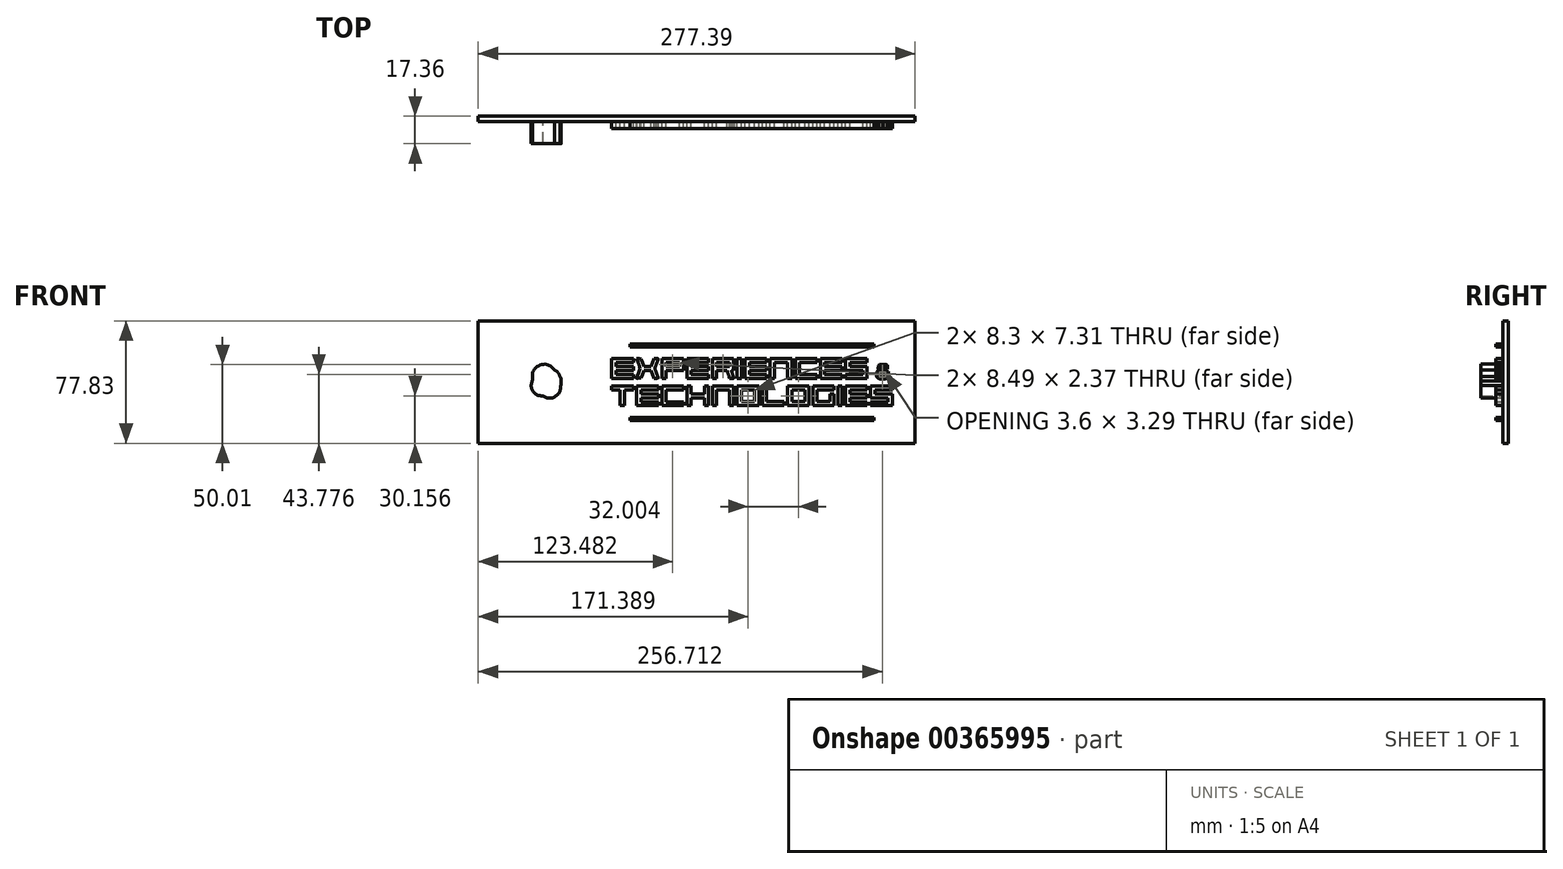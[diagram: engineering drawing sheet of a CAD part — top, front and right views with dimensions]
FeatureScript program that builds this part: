
annotation { "Feature Type Name" : "Feature", "Feature Type Description" : "" }
export const myFeature = defineFeature(function(context is Context, id is Id, definition is map)
    precondition{}
    {
        {
            var Q0;
            Q0=qCreatedBy(makeId("Front.planeOp"),FACE);
            var sketch = newSketch(context, id + "F0", { "sketchPlane" : qUnion([Q0])});
            skFitSpline(sketch, "E0", {"points": [v(-202.29, -52.1) * mm, v(-202.63, -51.97) * mm, v(-207.23, -47.55) * mm, v(-212.5, -42.27) * mm]});
            skLineSegment(sketch, "E1", {"start": v(-212.5, -42.27) * mm, "end": v(-222.07, -32.68) * mm});
            skLineSegment(sketch, "E2", {"start": v(-222.07, -32.68) * mm, "end": v(-222.07, 0) * mm});
            skLineSegment(sketch, "E3", {"start": v(-222.07, 0) * mm, "end": v(-222.06, 32.69) * mm});
            skLineSegment(sketch, "E4", {"start": v(-222.06, 32.69) * mm, "end": v(-212.25, 42.46) * mm});
            skLineSegment(sketch, "E5", {"start": v(-212.25, 42.46) * mm, "end": v(-202.45, 52.24) * mm});
            skLineSegment(sketch, "E6", {"start": v(-202.45, 52.24) * mm, "end": v(-163.97, 52.26) * mm});
            skFitSpline(sketch, "E7", {"points": [v(-163.97, 52.26) * mm, v(-141.12, 52.27) * mm, v(-125.15, 52.15) * mm, v(-124.66, 51.95) * mm]});
            skFitSpline(sketch, "E8", {"points": [v(-124.66, 51.95) * mm, v(-123.83, 51.63) * mm, v(-104.06, 32.01) * mm, v(-103.43, 30.9) * mm]});
            skFitSpline(sketch, "E9", {"points": [v(-103.43, 30.9) * mm, v(-103.17, 30.42) * mm, v(-104.47, 28.94) * mm, v(-110.36, 23.07) * mm]});
            skFitSpline(sketch, "E10", {"points": [v(-110.36, 23.07) * mm, v(-118.62, 14.84) * mm, v(-117.53, 15.3) * mm, v(-120.97, 18.54) * mm]});
            skFitSpline(sketch, "E11", {"points": [v(-120.97, 18.54) * mm, v(-124.99, 22.33) * mm, v(-133.5, 27.21) * mm, v(-139.35, 29.1) * mm]});
            skFitSpline(sketch, "E12", {"points": [v(-139.35, 29.1) * mm, v(-147.14, 31.6) * mm, v(-149.04, 31.85) * mm, v(-161.22, 32) * mm]});
            skFitSpline(sketch, "E13", {"points": [v(-161.22, 32) * mm, v(-175.01, 32.17) * mm, v(-177.89, 31.75) * mm, v(-184.15, 28.62) * mm]});
            skFitSpline(sketch, "E14", {"points": [v(-184.15, 28.62) * mm, v(-187.85, 26.77) * mm, v(-191.88, 23.86) * mm, v(-191.53, 23.3) * mm]});
            skFitSpline(sketch, "E15", {"points": [v(-191.53, 23.3) * mm, v(-191.42, 23.12) * mm, v(-191.5, 23.01) * mm, v(-191.7, 23.07) * mm]});
            skFitSpline(sketch, "E16", {"points": [v(-191.7, 23.07) * mm, v(-192.32, 23.23) * mm, v(-195.74, 19.26) * mm, v(-197.53, 16.3) * mm]});
            skFitSpline(sketch, "E17", {"points": [v(-197.53, 16.3) * mm, v(-203.86, 5.82) * mm, v(-203.4, -8.29) * mm, v(-196.42, -18.2) * mm]});
            skFitSpline(sketch, "E18", {"points": [v(-196.42, -18.2) * mm, v(-194.67, -20.7) * mm, v(-189.4, -26.05) * mm, v(-188.72, -26.05) * mm]});
            skFitSpline(sketch, "E19", {"points": [v(-188.72, -26.05) * mm, v(-188.47, -26.05) * mm, v(-188.21, -26.17) * mm, v(-188.15, -26.32) * mm]});
            skFitSpline(sketch, "E20", {"points": [v(-188.15, -26.32) * mm, v(-187.87, -26.95) * mm, v(-184.27, -28.92) * mm, v(-181.26, -30.08) * mm]});
            skFitSpline(sketch, "E21", {"points": [v(-181.26, -30.08) * mm, v(-176.54, -31.9) * mm, v(-172.16, -32.44) * mm, v(-162.45, -32.36) * mm]});
            skFitSpline(sketch, "E22", {"points": [v(-162.45, -32.36) * mm, v(-158.09, -32.32) * mm, v(-153.33, -32.15) * mm, v(-151.87, -31.98) * mm]});
            skFitSpline(sketch, "E23", {"points": [v(-151.87, -31.98) * mm, v(-139.35, -30.48) * mm, v(-129.8, -26.35) * mm, v(-120.76, -18.54) * mm]});
            skFitSpline(sketch, "E24", {"points": [v(-120.76, -18.54) * mm, v(-119.22, -17.21) * mm, v(-117.82, -16.18) * mm, v(-117.64, -16.24) * mm]});
            skFitSpline(sketch, "E25", {"points": [v(-117.64, -16.24) * mm, v(-117.06, -16.44) * mm, v(-103.55, -30.05) * mm, v(-103.37, -30.62) * mm]});
            skFitSpline(sketch, "E26", {"points": [v(-103.37, -30.62) * mm, v(-103.25, -31) * mm, v(-106.53, -34.5) * mm, v(-113.69, -41.67) * mm]});
            skLineSegment(sketch, "E27", {"start": v(-113.69, -41.67) * mm, "end": v(-124.19, -52.16) * mm});
            skLineSegment(sketch, "E28", {"start": v(-124.19, -52.16) * mm, "end": v(-162.92, -52.25) * mm});
            skFitSpline(sketch, "E29", {"points": [v(-162.92, -52.25) * mm, v(-184.22, -52.3) * mm, v(-201.94, -52.23) * mm, v(-202.29, -52.1) * mm]});
            skLineSegment(sketch, "E30", {"start": v(-202.29, -52.1) * mm, "end": v(-202.29, -52.1) * mm});
            skLineSegment(sketch, "E31", {"start": v(-75.67, -41.75) * mm, "end": v(-75.67, -40.16) * mm});
            skLineSegment(sketch, "E32", {"start": v(-75.67, -40.16) * mm, "end": v(62.8, -40.16) * mm});
            skLineSegment(sketch, "E33", {"start": v(62.8, -40.16) * mm, "end": v(201.26, -40.16) * mm});
            skLineSegment(sketch, "E34", {"start": v(201.26, -40.16) * mm, "end": v(201.26, -41.75) * mm});
            skLineSegment(sketch, "E35", {"start": v(201.26, -41.75) * mm, "end": v(201.26, -43.34) * mm});
            skLineSegment(sketch, "E36", {"start": v(201.26, -43.34) * mm, "end": v(62.8, -43.34) * mm});
            skLineSegment(sketch, "E37", {"start": v(62.8, -43.34) * mm, "end": v(-75.67, -43.34) * mm});
            skLineSegment(sketch, "E38", {"start": v(-75.67, -43.34) * mm, "end": v(-75.67, -41.75) * mm});
            skLineSegment(sketch, "E39", {"start": v(-86.6, -17.94) * mm, "end": v(-86.6, -9.12) * mm});
            skLineSegment(sketch, "E40", {"start": v(-86.6, -9.12) * mm, "end": v(-91.55, -9.12) * mm});
            skLineSegment(sketch, "E41", {"start": v(-91.55, -9.12) * mm, "end": v(-96.48, -9.12) * mm});
            skLineSegment(sketch, "E42", {"start": v(-96.48, -9.12) * mm, "end": v(-96.48, -6.82) * mm});
            skLineSegment(sketch, "E43", {"start": v(-96.48, -6.82) * mm, "end": v(-96.48, -4.53) * mm});
            skLineSegment(sketch, "E44", {"start": v(-96.48, -4.53) * mm, "end": v(-84.14, -4.53) * mm});
            skLineSegment(sketch, "E45", {"start": v(-84.14, -4.53) * mm, "end": v(-71.8, -4.53) * mm});
            skLineSegment(sketch, "E46", {"start": v(-71.8, -4.53) * mm, "end": v(-71.8, -6.82) * mm});
            skLineSegment(sketch, "E47", {"start": v(-71.8, -6.82) * mm, "end": v(-71.8, -9.12) * mm});
            skLineSegment(sketch, "E48", {"start": v(-71.8, -9.12) * mm, "end": v(-76.73, -9.12) * mm});
            skLineSegment(sketch, "E49", {"start": v(-76.73, -9.12) * mm, "end": v(-81.67, -9.12) * mm});
            skLineSegment(sketch, "E50", {"start": v(-81.67, -9.12) * mm, "end": v(-81.67, -17.94) * mm});
            skLineSegment(sketch, "E51", {"start": v(-81.67, -17.94) * mm, "end": v(-81.67, -26.76) * mm});
            skLineSegment(sketch, "E52", {"start": v(-81.67, -26.76) * mm, "end": v(-84.14, -26.76) * mm});
            skLineSegment(sketch, "E53", {"start": v(-84.14, -26.76) * mm, "end": v(-86.6, -26.76) * mm});
            skLineSegment(sketch, "E54", {"start": v(-86.6, -26.76) * mm, "end": v(-86.6, -17.94) * mm});
            skLineSegment(sketch, "E55", {"start": v(-67.9, -15.64) * mm, "end": v(-67.9, -4.53) * mm});
            skLineSegment(sketch, "E56", {"start": v(-67.9, -4.53) * mm, "end": v(-55.56, -4.53) * mm});
            skLineSegment(sketch, "E57", {"start": v(-55.56, -4.53) * mm, "end": v(-43.22, -4.53) * mm});
            skLineSegment(sketch, "E58", {"start": v(-43.22, -4.53) * mm, "end": v(-43.22, -6.82) * mm});
            skLineSegment(sketch, "E59", {"start": v(-43.22, -6.82) * mm, "end": v(-43.22, -9.12) * mm});
            skLineSegment(sketch, "E60", {"start": v(-43.22, -9.12) * mm, "end": v(-53.1, -9.12) * mm});
            skLineSegment(sketch, "E61", {"start": v(-53.1, -9.12) * mm, "end": v(-62.97, -9.12) * mm});
            skLineSegment(sketch, "E62", {"start": v(-62.97, -9.12) * mm, "end": v(-62.97, -11.23) * mm});
            skLineSegment(sketch, "E63", {"start": v(-62.97, -11.23) * mm, "end": v(-62.97, -13.35) * mm});
            skLineSegment(sketch, "E64", {"start": v(-62.97, -13.35) * mm, "end": v(-53.1, -13.35) * mm});
            skLineSegment(sketch, "E65", {"start": v(-53.1, -13.35) * mm, "end": v(-43.22, -13.35) * mm});
            skLineSegment(sketch, "E66", {"start": v(-43.22, -13.35) * mm, "end": v(-43.22, -15.64) * mm});
            skLineSegment(sketch, "E67", {"start": v(-43.22, -15.64) * mm, "end": v(-43.22, -17.94) * mm});
            skLineSegment(sketch, "E68", {"start": v(-43.22, -17.94) * mm, "end": v(-53.1, -17.94) * mm});
            skLineSegment(sketch, "E69", {"start": v(-53.1, -17.94) * mm, "end": v(-62.97, -17.94) * mm});
            skLineSegment(sketch, "E70", {"start": v(-62.97, -17.94) * mm, "end": v(-62.97, -20.23) * mm});
            skLineSegment(sketch, "E71", {"start": v(-62.97, -20.23) * mm, "end": v(-62.97, -22.52) * mm});
            skLineSegment(sketch, "E72", {"start": v(-62.97, -22.52) * mm, "end": v(-53.1, -22.52) * mm});
            skLineSegment(sketch, "E73", {"start": v(-53.1, -22.52) * mm, "end": v(-43.22, -22.52) * mm});
            skLineSegment(sketch, "E74", {"start": v(-43.22, -22.52) * mm, "end": v(-43.22, -24.64) * mm});
            skLineSegment(sketch, "E75", {"start": v(-43.22, -24.64) * mm, "end": v(-43.22, -26.76) * mm});
            skLineSegment(sketch, "E76", {"start": v(-43.22, -26.76) * mm, "end": v(-55.56, -26.76) * mm});
            skLineSegment(sketch, "E77", {"start": v(-55.56, -26.76) * mm, "end": v(-67.9, -26.76) * mm});
            skLineSegment(sketch, "E78", {"start": v(-67.9, -26.76) * mm, "end": v(-67.9, -15.64) * mm});
            skLineSegment(sketch, "E79", {"start": v(-39.33, -15.64) * mm, "end": v(-39.33, -4.53) * mm});
            skLineSegment(sketch, "E80", {"start": v(-39.33, -4.53) * mm, "end": v(-27.16, -4.53) * mm});
            skLineSegment(sketch, "E81", {"start": v(-27.16, -4.53) * mm, "end": v(-15, -4.53) * mm});
            skLineSegment(sketch, "E82", {"start": v(-15, -4.53) * mm, "end": v(-15, -6.82) * mm});
            skLineSegment(sketch, "E83", {"start": v(-15, -6.82) * mm, "end": v(-15, -9.12) * mm});
            skLineSegment(sketch, "E84", {"start": v(-15, -9.12) * mm, "end": v(-24.87, -9.12) * mm});
            skLineSegment(sketch, "E85", {"start": v(-24.87, -9.12) * mm, "end": v(-34.75, -9.12) * mm});
            skLineSegment(sketch, "E86", {"start": v(-34.75, -9.12) * mm, "end": v(-34.75, -15.82) * mm});
            skLineSegment(sketch, "E87", {"start": v(-34.75, -15.82) * mm, "end": v(-34.75, -22.52) * mm});
            skLineSegment(sketch, "E88", {"start": v(-34.75, -22.52) * mm, "end": v(-24.87, -22.52) * mm});
            skLineSegment(sketch, "E89", {"start": v(-24.87, -22.52) * mm, "end": v(-15, -22.52) * mm});
            skLineSegment(sketch, "E90", {"start": v(-15, -22.52) * mm, "end": v(-15, -24.64) * mm});
            skLineSegment(sketch, "E91", {"start": v(-15, -24.64) * mm, "end": v(-15, -26.76) * mm});
            skLineSegment(sketch, "E92", {"start": v(-15, -26.76) * mm, "end": v(-27.16, -26.76) * mm});
            skLineSegment(sketch, "E93", {"start": v(-27.16, -26.76) * mm, "end": v(-39.33, -26.76) * mm});
            skLineSegment(sketch, "E94", {"start": v(-39.33, -26.76) * mm, "end": v(-39.33, -15.64) * mm});
            skLineSegment(sketch, "E95", {"start": v(-10.76, -15.64) * mm, "end": v(-10.76, -4.53) * mm});
            skLineSegment(sketch, "E96", {"start": v(-10.76, -4.53) * mm, "end": v(-8.47, -4.53) * mm});
            skLineSegment(sketch, "E97", {"start": v(-8.47, -4.53) * mm, "end": v(-6.17, -4.53) * mm});
            skLineSegment(sketch, "E98", {"start": v(-6.17, -4.53) * mm, "end": v(-6.17, -8.94) * mm});
            skLineSegment(sketch, "E99", {"start": v(-6.17, -8.94) * mm, "end": v(-6.17, -13.35) * mm});
            skLineSegment(sketch, "E100", {"start": v(-6.17, -13.35) * mm, "end": v(1.41, -13.35) * mm});
            skLineSegment(sketch, "E101", {"start": v(1.41, -13.35) * mm, "end": v(9, -13.35) * mm});
            skLineSegment(sketch, "E102", {"start": v(9, -13.35) * mm, "end": v(9, -8.94) * mm});
            skLineSegment(sketch, "E103", {"start": v(9, -8.94) * mm, "end": v(9, -4.53) * mm});
            skLineSegment(sketch, "E104", {"start": v(9, -4.53) * mm, "end": v(11.29, -4.53) * mm});
            skLineSegment(sketch, "E105", {"start": v(11.29, -4.53) * mm, "end": v(13.58, -4.53) * mm});
            skLineSegment(sketch, "E106", {"start": v(13.58, -4.53) * mm, "end": v(13.58, -15.64) * mm});
            skLineSegment(sketch, "E107", {"start": v(13.58, -15.64) * mm, "end": v(13.58, -26.76) * mm});
            skLineSegment(sketch, "E108", {"start": v(13.58, -26.76) * mm, "end": v(11.29, -26.76) * mm});
            skLineSegment(sketch, "E109", {"start": v(11.29, -26.76) * mm, "end": v(9, -26.76) * mm});
            skLineSegment(sketch, "E110", {"start": v(9, -26.76) * mm, "end": v(9, -22.35) * mm});
            skLineSegment(sketch, "E111", {"start": v(9, -22.35) * mm, "end": v(9, -17.94) * mm});
            skLineSegment(sketch, "E112", {"start": v(9, -17.94) * mm, "end": v(1.41, -17.94) * mm});
            skLineSegment(sketch, "E113", {"start": v(1.41, -17.94) * mm, "end": v(-6.17, -17.94) * mm});
            skLineSegment(sketch, "E114", {"start": v(-6.17, -17.94) * mm, "end": v(-6.17, -22.35) * mm});
            skLineSegment(sketch, "E115", {"start": v(-6.17, -22.35) * mm, "end": v(-6.17, -26.76) * mm});
            skLineSegment(sketch, "E116", {"start": v(-6.17, -26.76) * mm, "end": v(-8.47, -26.76) * mm});
            skLineSegment(sketch, "E117", {"start": v(-8.47, -26.76) * mm, "end": v(-10.76, -26.76) * mm});
            skLineSegment(sketch, "E118", {"start": v(-10.76, -26.76) * mm, "end": v(-10.76, -15.64) * mm});
            skLineSegment(sketch, "E119", {"start": v(17.82, -15.64) * mm, "end": v(17.82, -4.53) * mm});
            skLineSegment(sketch, "E120", {"start": v(17.82, -4.53) * mm, "end": v(29.99, -4.53) * mm});
            skLineSegment(sketch, "E121", {"start": v(29.99, -4.53) * mm, "end": v(42.16, -4.53) * mm});
            skLineSegment(sketch, "E122", {"start": v(42.16, -4.53) * mm, "end": v(42.16, -15.64) * mm});
            skLineSegment(sketch, "E123", {"start": v(42.16, -15.64) * mm, "end": v(42.16, -26.76) * mm});
            skLineSegment(sketch, "E124", {"start": v(42.16, -26.76) * mm, "end": v(39.86, -26.76) * mm});
            skLineSegment(sketch, "E125", {"start": v(39.86, -26.76) * mm, "end": v(37.57, -26.76) * mm});
            skLineSegment(sketch, "E126", {"start": v(37.57, -26.76) * mm, "end": v(37.57, -17.94) * mm});
            skLineSegment(sketch, "E127", {"start": v(37.57, -17.94) * mm, "end": v(37.57, -9.12) * mm});
            skLineSegment(sketch, "E128", {"start": v(37.57, -9.12) * mm, "end": v(29.99, -9.12) * mm});
            skLineSegment(sketch, "E129", {"start": v(29.99, -9.12) * mm, "end": v(22.4, -9.12) * mm});
            skLineSegment(sketch, "E130", {"start": v(22.4, -9.12) * mm, "end": v(22.4, -17.94) * mm});
            skLineSegment(sketch, "E131", {"start": v(22.4, -17.94) * mm, "end": v(22.4, -26.76) * mm});
            skLineSegment(sketch, "E132", {"start": v(22.4, -26.76) * mm, "end": v(20.1, -26.76) * mm});
            skLineSegment(sketch, "E133", {"start": v(20.1, -26.76) * mm, "end": v(17.82, -26.76) * mm});
            skLineSegment(sketch, "E134", {"start": v(17.82, -26.76) * mm, "end": v(17.82, -15.64) * mm});
            skLineSegment(sketch, "E135", {"start": v(46.04, -15.64) * mm, "end": v(46.04, -4.53) * mm});
            skLineSegment(sketch, "E136", {"start": v(46.04, -4.53) * mm, "end": v(58.38, -4.53) * mm});
            skLineSegment(sketch, "E137", {"start": v(58.38, -4.53) * mm, "end": v(70.73, -4.53) * mm});
            skLineSegment(sketch, "E138", {"start": v(70.73, -4.53) * mm, "end": v(70.73, -15.64) * mm});
            skLineSegment(sketch, "E139", {"start": v(70.73, -15.64) * mm, "end": v(70.73, -26.76) * mm});
            skLineSegment(sketch, "E140", {"start": v(70.73, -26.76) * mm, "end": v(58.38, -26.76) * mm});
            skLineSegment(sketch, "E141", {"start": v(58.38, -26.76) * mm, "end": v(46.04, -26.76) * mm});
            skLineSegment(sketch, "E142", {"start": v(46.04, -26.76) * mm, "end": v(46.04, -15.64) * mm});
            skLineSegment(sketch, "E143", {"start": v(65.8, -15.64) * mm, "end": v(65.8, -9.12) * mm});
            skLineSegment(sketch, "E144", {"start": v(65.8, -9.12) * mm, "end": v(58.38, -9.12) * mm});
            skLineSegment(sketch, "E145", {"start": v(58.38, -9.12) * mm, "end": v(50.98, -9.12) * mm});
            skLineSegment(sketch, "E146", {"start": v(50.98, -9.12) * mm, "end": v(50.98, -15.64) * mm});
            skLineSegment(sketch, "E147", {"start": v(50.98, -15.64) * mm, "end": v(50.98, -22.17) * mm});
            skLineSegment(sketch, "E148", {"start": v(50.98, -22.17) * mm, "end": v(58.38, -22.17) * mm});
            skLineSegment(sketch, "E149", {"start": v(58.38, -22.17) * mm, "end": v(65.8, -22.17) * mm});
            skLineSegment(sketch, "E150", {"start": v(65.8, -22.17) * mm, "end": v(65.8, -15.64) * mm});
            skLineSegment(sketch, "E151", {"start": v(74.61, -15.64) * mm, "end": v(74.61, -4.53) * mm});
            skLineSegment(sketch, "E152", {"start": v(74.61, -4.53) * mm, "end": v(77.08, -4.53) * mm});
            skLineSegment(sketch, "E153", {"start": v(77.08, -4.53) * mm, "end": v(79.55, -4.53) * mm});
            skLineSegment(sketch, "E154", {"start": v(79.55, -4.53) * mm, "end": v(79.55, -13.35) * mm});
            skLineSegment(sketch, "E155", {"start": v(79.55, -13.35) * mm, "end": v(79.55, -22.17) * mm});
            skLineSegment(sketch, "E156", {"start": v(79.55, -22.17) * mm, "end": v(89.43, -22.17) * mm});
            skLineSegment(sketch, "E157", {"start": v(89.43, -22.17) * mm, "end": v(99.3, -22.17) * mm});
            skLineSegment(sketch, "E158", {"start": v(99.3, -22.17) * mm, "end": v(99.3, -24.46) * mm});
            skLineSegment(sketch, "E159", {"start": v(99.3, -24.46) * mm, "end": v(99.3, -26.76) * mm});
            skLineSegment(sketch, "E160", {"start": v(99.3, -26.76) * mm, "end": v(86.96, -26.76) * mm});
            skLineSegment(sketch, "E161", {"start": v(86.96, -26.76) * mm, "end": v(74.61, -26.76) * mm});
            skLineSegment(sketch, "E162", {"start": v(74.61, -26.76) * mm, "end": v(74.61, -15.64) * mm});
            skLineSegment(sketch, "E163", {"start": v(103.19, -15.64) * mm, "end": v(103.19, -4.53) * mm});
            skLineSegment(sketch, "E164", {"start": v(103.19, -4.53) * mm, "end": v(115.36, -4.53) * mm});
            skLineSegment(sketch, "E165", {"start": v(115.36, -4.53) * mm, "end": v(127.53, -4.53) * mm});
            skLineSegment(sketch, "E166", {"start": v(127.53, -4.53) * mm, "end": v(127.53, -15.64) * mm});
            skLineSegment(sketch, "E167", {"start": v(127.53, -15.64) * mm, "end": v(127.53, -26.76) * mm});
            skLineSegment(sketch, "E168", {"start": v(127.53, -26.76) * mm, "end": v(115.36, -26.76) * mm});
            skLineSegment(sketch, "E169", {"start": v(115.36, -26.76) * mm, "end": v(103.19, -26.76) * mm});
            skLineSegment(sketch, "E170", {"start": v(103.19, -26.76) * mm, "end": v(103.19, -15.64) * mm});
            skLineSegment(sketch, "E171", {"start": v(122.94, -15.64) * mm, "end": v(122.94, -9.12) * mm});
            skLineSegment(sketch, "E172", {"start": v(122.94, -9.12) * mm, "end": v(115.53, -9.12) * mm});
            skLineSegment(sketch, "E173", {"start": v(115.53, -9.12) * mm, "end": v(108.13, -9.12) * mm});
            skLineSegment(sketch, "E174", {"start": v(108.13, -9.12) * mm, "end": v(108.13, -15.64) * mm});
            skLineSegment(sketch, "E175", {"start": v(108.13, -15.64) * mm, "end": v(108.13, -22.17) * mm});
            skLineSegment(sketch, "E176", {"start": v(108.13, -22.17) * mm, "end": v(115.53, -22.17) * mm});
            skLineSegment(sketch, "E177", {"start": v(115.53, -22.17) * mm, "end": v(122.94, -22.17) * mm});
            skLineSegment(sketch, "E178", {"start": v(122.94, -22.17) * mm, "end": v(122.94, -15.64) * mm});
            skLineSegment(sketch, "E179", {"start": v(131.76, -15.64) * mm, "end": v(131.76, -4.53) * mm});
            skLineSegment(sketch, "E180", {"start": v(131.76, -4.53) * mm, "end": v(143.93, -4.53) * mm});
            skLineSegment(sketch, "E181", {"start": v(143.93, -4.53) * mm, "end": v(156.1, -4.53) * mm});
            skLineSegment(sketch, "E182", {"start": v(156.1, -4.53) * mm, "end": v(156.1, -6.82) * mm});
            skLineSegment(sketch, "E183", {"start": v(156.1, -6.82) * mm, "end": v(156.1, -9.12) * mm});
            skLineSegment(sketch, "E184", {"start": v(156.1, -9.12) * mm, "end": v(146.23, -9.12) * mm});
            skLineSegment(sketch, "E185", {"start": v(146.23, -9.12) * mm, "end": v(136.35, -9.12) * mm});
            skLineSegment(sketch, "E186", {"start": v(136.35, -9.12) * mm, "end": v(136.35, -15.64) * mm});
            skLineSegment(sketch, "E187", {"start": v(136.35, -15.64) * mm, "end": v(136.35, -22.17) * mm});
            skLineSegment(sketch, "E188", {"start": v(136.35, -22.17) * mm, "end": v(143.93, -22.17) * mm});
            skLineSegment(sketch, "E189", {"start": v(143.93, -22.17) * mm, "end": v(151.52, -22.17) * mm});
            skLineSegment(sketch, "E190", {"start": v(151.52, -22.17) * mm, "end": v(151.52, -17.76) * mm});
            skLineSegment(sketch, "E191", {"start": v(151.52, -17.76) * mm, "end": v(151.52, -13.35) * mm});
            skLineSegment(sketch, "E192", {"start": v(151.52, -13.35) * mm, "end": v(153.81, -13.35) * mm});
            skLineSegment(sketch, "E193", {"start": v(153.81, -13.35) * mm, "end": v(156.1, -13.35) * mm});
            skLineSegment(sketch, "E194", {"start": v(156.1, -13.35) * mm, "end": v(156.1, -20.05) * mm});
            skLineSegment(sketch, "E195", {"start": v(156.1, -20.05) * mm, "end": v(156.1, -26.76) * mm});
            skLineSegment(sketch, "E196", {"start": v(156.1, -26.76) * mm, "end": v(143.93, -26.76) * mm});
            skLineSegment(sketch, "E197", {"start": v(143.93, -26.76) * mm, "end": v(131.76, -26.76) * mm});
            skLineSegment(sketch, "E198", {"start": v(131.76, -26.76) * mm, "end": v(131.76, -15.64) * mm});
            skLineSegment(sketch, "E199", {"start": v(160.34, -15.64) * mm, "end": v(160.34, -4.53) * mm});
            skLineSegment(sketch, "E200", {"start": v(160.34, -4.53) * mm, "end": v(162.63, -4.53) * mm});
            skLineSegment(sketch, "E201", {"start": v(162.63, -4.53) * mm, "end": v(164.92, -4.53) * mm});
            skLineSegment(sketch, "E202", {"start": v(164.92, -4.53) * mm, "end": v(164.92, -15.64) * mm});
            skLineSegment(sketch, "E203", {"start": v(164.92, -15.64) * mm, "end": v(164.92, -26.76) * mm});
            skLineSegment(sketch, "E204", {"start": v(164.92, -26.76) * mm, "end": v(162.63, -26.76) * mm});
            skLineSegment(sketch, "E205", {"start": v(162.63, -26.76) * mm, "end": v(160.34, -26.76) * mm});
            skLineSegment(sketch, "E206", {"start": v(160.34, -26.76) * mm, "end": v(160.34, -15.64) * mm});
            skLineSegment(sketch, "E207", {"start": v(169.16, -15.64) * mm, "end": v(169.16, -4.53) * mm});
            skLineSegment(sketch, "E208", {"start": v(169.16, -4.53) * mm, "end": v(181.33, -4.53) * mm});
            skLineSegment(sketch, "E209", {"start": v(181.33, -4.53) * mm, "end": v(193.5, -4.53) * mm});
            skLineSegment(sketch, "E210", {"start": v(193.5, -4.53) * mm, "end": v(193.5, -6.82) * mm});
            skLineSegment(sketch, "E211", {"start": v(193.5, -6.82) * mm, "end": v(193.5, -9.12) * mm});
            skLineSegment(sketch, "E212", {"start": v(193.5, -9.12) * mm, "end": v(183.62, -9.12) * mm});
            skLineSegment(sketch, "E213", {"start": v(183.62, -9.12) * mm, "end": v(173.74, -9.12) * mm});
            skLineSegment(sketch, "E214", {"start": v(173.74, -9.12) * mm, "end": v(173.74, -11.23) * mm});
            skLineSegment(sketch, "E215", {"start": v(173.74, -11.23) * mm, "end": v(173.74, -13.35) * mm});
            skLineSegment(sketch, "E216", {"start": v(173.74, -13.35) * mm, "end": v(183.62, -13.35) * mm});
            skLineSegment(sketch, "E217", {"start": v(183.62, -13.35) * mm, "end": v(193.5, -13.35) * mm});
            skLineSegment(sketch, "E218", {"start": v(193.5, -13.35) * mm, "end": v(193.5, -15.64) * mm});
            skLineSegment(sketch, "E219", {"start": v(193.5, -15.64) * mm, "end": v(193.5, -17.94) * mm});
            skLineSegment(sketch, "E220", {"start": v(193.5, -17.94) * mm, "end": v(183.62, -17.94) * mm});
            skLineSegment(sketch, "E221", {"start": v(183.62, -17.94) * mm, "end": v(173.74, -17.94) * mm});
            skLineSegment(sketch, "E222", {"start": v(173.74, -17.94) * mm, "end": v(173.74, -20.23) * mm});
            skLineSegment(sketch, "E223", {"start": v(173.74, -20.23) * mm, "end": v(173.74, -22.52) * mm});
            skLineSegment(sketch, "E224", {"start": v(173.74, -22.52) * mm, "end": v(183.62, -22.52) * mm});
            skLineSegment(sketch, "E225", {"start": v(183.62, -22.52) * mm, "end": v(193.5, -22.52) * mm});
            skLineSegment(sketch, "E226", {"start": v(193.5, -22.52) * mm, "end": v(193.5, -24.64) * mm});
            skLineSegment(sketch, "E227", {"start": v(193.5, -24.64) * mm, "end": v(193.5, -26.76) * mm});
            skLineSegment(sketch, "E228", {"start": v(193.5, -26.76) * mm, "end": v(181.33, -26.76) * mm});
            skLineSegment(sketch, "E229", {"start": v(181.33, -26.76) * mm, "end": v(169.16, -26.76) * mm});
            skLineSegment(sketch, "E230", {"start": v(169.16, -26.76) * mm, "end": v(169.16, -15.64) * mm});
            skLineSegment(sketch, "E231", {"start": v(197.38, -24.64) * mm, "end": v(197.38, -22.52) * mm});
            skLineSegment(sketch, "E232", {"start": v(197.38, -22.52) * mm, "end": v(207.26, -22.52) * mm});
            skLineSegment(sketch, "E233", {"start": v(207.26, -22.52) * mm, "end": v(217.13, -22.52) * mm});
            skLineSegment(sketch, "E234", {"start": v(217.13, -22.52) * mm, "end": v(217.13, -20.23) * mm});
            skLineSegment(sketch, "E235", {"start": v(217.13, -20.23) * mm, "end": v(217.13, -17.94) * mm});
            skLineSegment(sketch, "E236", {"start": v(217.13, -17.94) * mm, "end": v(207.26, -17.94) * mm});
            skLineSegment(sketch, "E237", {"start": v(207.26, -17.94) * mm, "end": v(197.38, -17.94) * mm});
            skLineSegment(sketch, "E238", {"start": v(197.38, -17.94) * mm, "end": v(197.38, -11.23) * mm});
            skLineSegment(sketch, "E239", {"start": v(197.38, -11.23) * mm, "end": v(197.38, -4.53) * mm});
            skLineSegment(sketch, "E240", {"start": v(197.38, -4.53) * mm, "end": v(209.73, -4.53) * mm});
            skLineSegment(sketch, "E241", {"start": v(209.73, -4.53) * mm, "end": v(222.07, -4.53) * mm});
            skLineSegment(sketch, "E242", {"start": v(222.07, -4.53) * mm, "end": v(222.07, -6.82) * mm});
            skLineSegment(sketch, "E243", {"start": v(222.07, -6.82) * mm, "end": v(222.07, -9.12) * mm});
            skLineSegment(sketch, "E244", {"start": v(222.07, -9.12) * mm, "end": v(212.2, -9.12) * mm});
            skLineSegment(sketch, "E245", {"start": v(212.2, -9.12) * mm, "end": v(202.32, -9.12) * mm});
            skLineSegment(sketch, "E246", {"start": v(202.32, -9.12) * mm, "end": v(202.32, -11.23) * mm});
            skLineSegment(sketch, "E247", {"start": v(202.32, -11.23) * mm, "end": v(202.32, -13.35) * mm});
            skLineSegment(sketch, "E248", {"start": v(202.32, -13.35) * mm, "end": v(212.2, -13.35) * mm});
            skLineSegment(sketch, "E249", {"start": v(212.2, -13.35) * mm, "end": v(222.07, -13.35) * mm});
            skLineSegment(sketch, "E250", {"start": v(222.07, -13.35) * mm, "end": v(222.07, -20.05) * mm});
            skLineSegment(sketch, "E251", {"start": v(222.07, -20.05) * mm, "end": v(222.07, -26.76) * mm});
            skLineSegment(sketch, "E252", {"start": v(222.07, -26.76) * mm, "end": v(209.73, -26.76) * mm});
            skLineSegment(sketch, "E253", {"start": v(209.73, -26.76) * mm, "end": v(197.38, -26.76) * mm});
            skLineSegment(sketch, "E254", {"start": v(197.38, -26.76) * mm, "end": v(197.38, -24.64) * mm});
            skFitSpline(sketch, "E255", {"points": [v(-174.06, -15.97) * mm, v(-182.2, -13.78) * mm, v(-187.45, -5.82) * mm, v(-186.12, 2.32) * mm]});
            skFitSpline(sketch, "E256", {"points": [v(-186.12, 2.32) * mm, v(-184.17, 14.28) * mm, v(-171, 20.11) * mm, v(-160.84, 13.53) * mm]});
            skFitSpline(sketch, "E257", {"points": [v(-160.84, 13.53) * mm, v(-158.3, 11.88) * mm, v(-156.44, 9.67) * mm, v(-154.98, 6.56) * mm]});
            skFitSpline(sketch, "E258", {"points": [v(-154.98, 6.56) * mm, v(-154.07, 4.61) * mm, v(-153.86, 3.64) * mm, v(-153.71, 0.9) * mm]});
            skFitSpline(sketch, "E259", {"points": [v(-153.71, 0.9) * mm, v(-153.6, -1.2) * mm, v(-153.7, -3) * mm, v(-154, -4.08) * mm]});
            skFitSpline(sketch, "E260", {"points": [v(-154, -4.08) * mm, v(-156.34, -12.87) * mm, v(-165.48, -18.27) * mm, v(-174.06, -15.97) * mm]});
            skFitSpline(sketch, "E261", {"points": [v(206.94, 4.04) * mm, v(205.13, 4.68) * mm, v(204.38, 5.93) * mm, v(204.32, 8.41) * mm]});
            skFitSpline(sketch, "E262", {"points": [v(204.32, 8.41) * mm, v(204.27, 10.71) * mm, v(205, 12.34) * mm, v(206.25, 12.67) * mm]});
            skFitSpline(sketch, "E263", {"points": [v(206.25, 12.67) * mm, v(206.73, 12.8) * mm, v(206.87, 13.03) * mm, v(206.7, 13.42) * mm]});
            skFitSpline(sketch, "E264", {"points": [v(206.7, 13.42) * mm, v(205.82, 15.53) * mm, v(205.78, 15.8) * mm, v(206.18, 17.28) * mm]});
            skFitSpline(sketch, "E265", {"points": [v(206.18, 17.28) * mm, v(206.7, 19.18) * mm, v(207.97, 19.81) * mm, v(211.32, 19.81) * mm]});
            skFitSpline(sketch, "E266", {"points": [v(211.32, 19.81) * mm, v(215.03, 19.81) * mm, v(216.43, 18.75) * mm, v(216.43, 15.95) * mm]});
            skLineSegment(sketch, "E267", {"start": v(216.43, 15.95) * mm, "end": v(216.43, 14.52) * mm});
            skLineSegment(sketch, "E268", {"start": v(216.43, 14.52) * mm, "end": v(214.84, 14.52) * mm});
            skFitSpline(sketch, "E269", {"points": [v(214.84, 14.52) * mm, v(213.26, 14.52) * mm, v(213.25, 14.53) * mm, v(213.25, 15.75) * mm]});
            skFitSpline(sketch, "E270", {"points": [v(213.25, 15.75) * mm, v(213.25, 16.78) * mm, v(213.1, 17.01) * mm, v(212.32, 17.2) * mm]});
            skFitSpline(sketch, "E271", {"points": [v(212.32, 17.2) * mm, v(210.78, 17.6) * mm, v(209.57, 16.96) * mm, v(209.44, 15.7) * mm]});
            skFitSpline(sketch, "E272", {"points": [v(209.44, 15.7) * mm, v(209.35, 14.72) * mm, v(209.62, 14.36) * mm, v(212.09, 12.24) * mm]});
            skFitSpline(sketch, "E273", {"points": [v(212.09, 12.24) * mm, v(214.75, 9.96) * mm, v(214.85, 9.91) * mm, v(214.95, 10.79) * mm]});
            skFitSpline(sketch, "E274", {"points": [v(214.95, 10.79) * mm, v(215.05, 11.6) * mm, v(215.22, 11.7) * mm, v(216.48, 11.7) * mm]});
            skLineSegment(sketch, "E275", {"start": v(216.48, 11.7) * mm, "end": v(217.9, 11.7) * mm});
            skLineSegment(sketch, "E276", {"start": v(217.9, 11.7) * mm, "end": v(217.8, 9.53) * mm});
            skFitSpline(sketch, "E277", {"points": [v(217.8, 9.53) * mm, v(217.72, 7.55) * mm, v(217.8, 7.32) * mm, v(218.66, 6.68) * mm]});
            skFitSpline(sketch, "E278", {"points": [v(218.66, 6.68) * mm, v(219.78, 5.87) * mm, v(219.82, 5.46) * mm, v(218.88, 4.33) * mm]});
            skLineSegment(sketch, "E279", {"start": v(218.88, 4.33) * mm, "end": v(218.17, 3.48) * mm});
            skLineSegment(sketch, "E280", {"start": v(218.17, 3.48) * mm, "end": v(217.37, 4.23) * mm});
            skLineSegment(sketch, "E281", {"start": v(217.37, 4.23) * mm, "end": v(216.57, 4.99) * mm});
            skLineSegment(sketch, "E282", {"start": v(216.57, 4.99) * mm, "end": v(215.19, 4.29) * mm});
            skFitSpline(sketch, "E283", {"points": [v(215.19, 4.29) * mm, v(213.59, 3.47) * mm, v(208.96, 3.33) * mm, v(206.94, 4.04) * mm]});
            skFitSpline(sketch, "E284", {"points": [v(213.05, 6.4) * mm, v(213.55, 6.59) * mm, v(213.95, 6.86) * mm, v(213.94, 7.01) * mm]});
            skFitSpline(sketch, "E285", {"points": [v(213.94, 7.01) * mm, v(213.92, 7.28) * mm, v(210.1, 10.53) * mm, v(209.12, 11.1) * mm]});
            skFitSpline(sketch, "E286", {"points": [v(209.12, 11.1) * mm, v(208.26, 11.62) * mm, v(207.6, 10.67) * mm, v(207.62, 8.92) * mm]});
            skFitSpline(sketch, "E287", {"points": [v(207.62, 8.92) * mm, v(207.62, 8.02) * mm, v(207.74, 7.1) * mm, v(207.88, 6.89) * mm]});
            skFitSpline(sketch, "E288", {"points": [v(207.88, 6.89) * mm, v(208.39, 6.1) * mm, v(211.5, 5.8) * mm, v(213.05, 6.4) * mm]});
            skLineSegment(sketch, "E289", {"start": v(-96.48, 15.4) * mm, "end": v(-96.48, 26.51) * mm});
            skLineSegment(sketch, "E290", {"start": v(-96.48, 26.51) * mm, "end": v(-84.14, 26.51) * mm});
            skLineSegment(sketch, "E291", {"start": v(-84.14, 26.51) * mm, "end": v(-71.8, 26.51) * mm});
            skLineSegment(sketch, "E292", {"start": v(-71.8, 26.51) * mm, "end": v(-71.8, 24.22) * mm});
            skLineSegment(sketch, "E293", {"start": v(-71.8, 24.22) * mm, "end": v(-71.8, 21.93) * mm});
            skLineSegment(sketch, "E294", {"start": v(-71.8, 21.93) * mm, "end": v(-81.67, 21.93) * mm});
            skLineSegment(sketch, "E295", {"start": v(-81.67, 21.93) * mm, "end": v(-91.55, 21.93) * mm});
            skLineSegment(sketch, "E296", {"start": v(-91.55, 21.93) * mm, "end": v(-91.55, 19.81) * mm});
            skLineSegment(sketch, "E297", {"start": v(-91.55, 19.81) * mm, "end": v(-91.55, 17.7) * mm});
            skLineSegment(sketch, "E298", {"start": v(-91.55, 17.7) * mm, "end": v(-81.67, 17.7) * mm});
            skLineSegment(sketch, "E299", {"start": v(-81.67, 17.7) * mm, "end": v(-71.8, 17.7) * mm});
            skLineSegment(sketch, "E300", {"start": v(-71.8, 17.7) * mm, "end": v(-71.8, 15.4) * mm});
            skLineSegment(sketch, "E301", {"start": v(-71.8, 15.4) * mm, "end": v(-71.8, 13.1) * mm});
            skLineSegment(sketch, "E302", {"start": v(-71.8, 13.1) * mm, "end": v(-81.67, 13.1) * mm});
            skLineSegment(sketch, "E303", {"start": v(-81.67, 13.1) * mm, "end": v(-91.55, 13.1) * mm});
            skLineSegment(sketch, "E304", {"start": v(-91.55, 13.1) * mm, "end": v(-91.55, 10.82) * mm});
            skLineSegment(sketch, "E305", {"start": v(-91.55, 10.82) * mm, "end": v(-91.55, 8.52) * mm});
            skLineSegment(sketch, "E306", {"start": v(-91.55, 8.52) * mm, "end": v(-81.67, 8.52) * mm});
            skLineSegment(sketch, "E307", {"start": v(-81.67, 8.52) * mm, "end": v(-71.8, 8.52) * mm});
            skLineSegment(sketch, "E308", {"start": v(-71.8, 8.52) * mm, "end": v(-71.8, 6.4) * mm});
            skLineSegment(sketch, "E309", {"start": v(-71.8, 6.4) * mm, "end": v(-71.8, 4.29) * mm});
            skLineSegment(sketch, "E310", {"start": v(-71.8, 4.29) * mm, "end": v(-84.14, 4.29) * mm});
            skLineSegment(sketch, "E311", {"start": v(-84.14, 4.29) * mm, "end": v(-96.48, 4.29) * mm});
            skLineSegment(sketch, "E312", {"start": v(-96.48, 4.29) * mm, "end": v(-96.48, 15.4) * mm});
            skFitSpline(sketch, "E313", {"points": [v(-67.83, 4.71) * mm, v(-67.74, 4.96) * mm, v(-66.82, 7.45) * mm, v(-65.8, 10.24) * mm]});
            skLineSegment(sketch, "E314", {"start": v(-65.8, 10.24) * mm, "end": v(-63.92, 15.3) * mm});
            skLineSegment(sketch, "E315", {"start": v(-63.92, 15.3) * mm, "end": v(-64.46, 16.94) * mm});
            skFitSpline(sketch, "E316", {"points": [v(-64.46, 16.94) * mm, v(-64.76, 17.84) * mm, v(-65.66, 20.37) * mm, v(-66.45, 22.56) * mm]});
            skLineSegment(sketch, "E317", {"start": v(-66.45, 22.56) * mm, "end": v(-67.9, 26.54) * mm});
            skLineSegment(sketch, "E318", {"start": v(-67.9, 26.54) * mm, "end": v(-65.37, 26.44) * mm});
            skLineSegment(sketch, "E319", {"start": v(-65.37, 26.44) * mm, "end": v(-62.84, 26.34) * mm});
            skLineSegment(sketch, "E320", {"start": v(-62.84, 26.34) * mm, "end": v(-61.25, 22) * mm});
            skLineSegment(sketch, "E321", {"start": v(-61.25, 22) * mm, "end": v(-59.67, 17.67) * mm});
            skLineSegment(sketch, "E322", {"start": v(-59.67, 17.67) * mm, "end": v(-55.59, 17.77) * mm});
            skLineSegment(sketch, "E323", {"start": v(-55.59, 17.77) * mm, "end": v(-51.5, 17.87) * mm});
            skLineSegment(sketch, "E324", {"start": v(-51.5, 17.87) * mm, "end": v(-49.96, 22.2) * mm});
            skLineSegment(sketch, "E325", {"start": v(-49.96, 22.2) * mm, "end": v(-48.4, 26.51) * mm});
            skLineSegment(sketch, "E326", {"start": v(-48.4, 26.51) * mm, "end": v(-45.99, 26.51) * mm});
            skFitSpline(sketch, "E327", {"points": [v(-45.99, 26.51) * mm, v(-44.66, 26.51) * mm, v(-43.57, 26.37) * mm, v(-43.57, 26.2) * mm]});
            skFitSpline(sketch, "E328", {"points": [v(-43.57, 26.2) * mm, v(-43.57, 26.01) * mm, v(-44.38, 23.67) * mm, v(-45.37, 20.99) * mm]});
            skFitSpline(sketch, "E329", {"points": [v(-45.37, 20.99) * mm, v(-46.35, 18.3) * mm, v(-47.16, 15.79) * mm, v(-47.16, 15.4) * mm]});
            skFitSpline(sketch, "E330", {"points": [v(-47.16, 15.4) * mm, v(-47.16, 15.01) * mm, v(-46.35, 12.5) * mm, v(-45.37, 9.81) * mm]});
            skFitSpline(sketch, "E331", {"points": [v(-45.37, 9.81) * mm, v(-44.38, 7.13) * mm, v(-43.57, 4.79) * mm, v(-43.57, 4.61) * mm]});
            skFitSpline(sketch, "E332", {"points": [v(-43.57, 4.61) * mm, v(-43.57, 4.43) * mm, v(-44.65, 4.29) * mm, v(-45.97, 4.29) * mm]});
            skLineSegment(sketch, "E333", {"start": v(-45.97, 4.29) * mm, "end": v(-48.37, 4.29) * mm});
            skLineSegment(sketch, "E334", {"start": v(-48.37, 4.29) * mm, "end": v(-49.94, 8.7) * mm});
            skLineSegment(sketch, "E335", {"start": v(-49.94, 8.7) * mm, "end": v(-51.5, 13.1) * mm});
            skLineSegment(sketch, "E336", {"start": v(-51.5, 13.1) * mm, "end": v(-55.6, 13.1) * mm});
            skLineSegment(sketch, "E337", {"start": v(-55.6, 13.1) * mm, "end": v(-59.7, 13.1) * mm});
            skLineSegment(sketch, "E338", {"start": v(-59.7, 13.1) * mm, "end": v(-61.27, 8.79) * mm});
            skLineSegment(sketch, "E339", {"start": v(-61.27, 8.79) * mm, "end": v(-62.85, 4.47) * mm});
            skLineSegment(sketch, "E340", {"start": v(-62.85, 4.47) * mm, "end": v(-65.42, 4.36) * mm});
            skFitSpline(sketch, "E341", {"points": [v(-65.42, 4.36) * mm, v(-67.42, 4.28) * mm, v(-67.96, 4.36) * mm, v(-67.83, 4.71) * mm]});
            skLineSegment(sketch, "E342", {"start": v(-67.83, 4.71) * mm, "end": v(-67.83, 4.71) * mm});
            skLineSegment(sketch, "E343", {"start": v(-39.33, 15.4) * mm, "end": v(-39.33, 26.51) * mm});
            skLineSegment(sketch, "E344", {"start": v(-39.33, 26.51) * mm, "end": v(-27.16, 26.51) * mm});
            skLineSegment(sketch, "E345", {"start": v(-27.16, 26.51) * mm, "end": v(-15, 26.51) * mm});
            skLineSegment(sketch, "E346", {"start": v(-15, 26.51) * mm, "end": v(-15, 19.81) * mm});
            skLineSegment(sketch, "E347", {"start": v(-15, 19.81) * mm, "end": v(-15, 13.1) * mm});
            skLineSegment(sketch, "E348", {"start": v(-15, 13.1) * mm, "end": v(-24.87, 13.1) * mm});
            skLineSegment(sketch, "E349", {"start": v(-24.87, 13.1) * mm, "end": v(-34.75, 13.1) * mm});
            skLineSegment(sketch, "E350", {"start": v(-34.75, 13.1) * mm, "end": v(-34.75, 8.7) * mm});
            skLineSegment(sketch, "E351", {"start": v(-34.75, 8.7) * mm, "end": v(-34.75, 4.29) * mm});
            skLineSegment(sketch, "E352", {"start": v(-34.75, 4.29) * mm, "end": v(-37.04, 4.29) * mm});
            skLineSegment(sketch, "E353", {"start": v(-37.04, 4.29) * mm, "end": v(-39.33, 4.29) * mm});
            skLineSegment(sketch, "E354", {"start": v(-39.33, 4.29) * mm, "end": v(-39.33, 15.4) * mm});
            skLineSegment(sketch, "E355", {"start": v(-19.58, 19.81) * mm, "end": v(-19.58, 21.93) * mm});
            skLineSegment(sketch, "E356", {"start": v(-19.58, 21.93) * mm, "end": v(-27.16, 21.93) * mm});
            skLineSegment(sketch, "E357", {"start": v(-27.16, 21.93) * mm, "end": v(-34.75, 21.93) * mm});
            skLineSegment(sketch, "E358", {"start": v(-34.75, 21.93) * mm, "end": v(-34.75, 19.81) * mm});
            skLineSegment(sketch, "E359", {"start": v(-34.75, 19.81) * mm, "end": v(-34.75, 17.7) * mm});
            skLineSegment(sketch, "E360", {"start": v(-34.75, 17.7) * mm, "end": v(-27.16, 17.7) * mm});
            skLineSegment(sketch, "E361", {"start": v(-27.16, 17.7) * mm, "end": v(-19.58, 17.7) * mm});
            skLineSegment(sketch, "E362", {"start": v(-19.58, 17.7) * mm, "end": v(-19.58, 19.81) * mm});
            skLineSegment(sketch, "E363", {"start": v(-10.76, 15.4) * mm, "end": v(-10.76, 26.51) * mm});
            skLineSegment(sketch, "E364", {"start": v(-10.76, 26.51) * mm, "end": v(1.41, 26.51) * mm});
            skLineSegment(sketch, "E365", {"start": v(1.41, 26.51) * mm, "end": v(13.58, 26.51) * mm});
            skLineSegment(sketch, "E366", {"start": v(13.58, 26.51) * mm, "end": v(13.58, 24.22) * mm});
            skLineSegment(sketch, "E367", {"start": v(13.58, 24.22) * mm, "end": v(13.58, 21.93) * mm});
            skLineSegment(sketch, "E368", {"start": v(13.58, 21.93) * mm, "end": v(3.7, 21.93) * mm});
            skLineSegment(sketch, "E369", {"start": v(3.7, 21.93) * mm, "end": v(-6.17, 21.93) * mm});
            skLineSegment(sketch, "E370", {"start": v(-6.17, 21.93) * mm, "end": v(-6.17, 19.81) * mm});
            skLineSegment(sketch, "E371", {"start": v(-6.17, 19.81) * mm, "end": v(-6.17, 17.7) * mm});
            skLineSegment(sketch, "E372", {"start": v(-6.17, 17.7) * mm, "end": v(3.7, 17.7) * mm});
            skLineSegment(sketch, "E373", {"start": v(3.7, 17.7) * mm, "end": v(13.58, 17.7) * mm});
            skLineSegment(sketch, "E374", {"start": v(13.58, 17.7) * mm, "end": v(13.58, 15.4) * mm});
            skLineSegment(sketch, "E375", {"start": v(13.58, 15.4) * mm, "end": v(13.58, 13.1) * mm});
            skLineSegment(sketch, "E376", {"start": v(13.58, 13.1) * mm, "end": v(3.7, 13.1) * mm});
            skLineSegment(sketch, "E377", {"start": v(3.7, 13.1) * mm, "end": v(-6.17, 13.1) * mm});
            skLineSegment(sketch, "E378", {"start": v(-6.17, 13.1) * mm, "end": v(-6.17, 10.82) * mm});
            skLineSegment(sketch, "E379", {"start": v(-6.17, 10.82) * mm, "end": v(-6.17, 8.52) * mm});
            skLineSegment(sketch, "E380", {"start": v(-6.17, 8.52) * mm, "end": v(3.7, 8.52) * mm});
            skLineSegment(sketch, "E381", {"start": v(3.7, 8.52) * mm, "end": v(13.58, 8.52) * mm});
            skLineSegment(sketch, "E382", {"start": v(13.58, 8.52) * mm, "end": v(13.58, 6.4) * mm});
            skLineSegment(sketch, "E383", {"start": v(13.58, 6.4) * mm, "end": v(13.58, 4.29) * mm});
            skLineSegment(sketch, "E384", {"start": v(13.58, 4.29) * mm, "end": v(1.41, 4.29) * mm});
            skLineSegment(sketch, "E385", {"start": v(1.41, 4.29) * mm, "end": v(-10.76, 4.29) * mm});
            skLineSegment(sketch, "E386", {"start": v(-10.76, 4.29) * mm, "end": v(-10.76, 15.4) * mm});
            skLineSegment(sketch, "E387", {"start": v(17.82, 15.4) * mm, "end": v(17.82, 26.51) * mm});
            skLineSegment(sketch, "E388", {"start": v(17.82, 26.51) * mm, "end": v(29.99, 26.51) * mm});
            skLineSegment(sketch, "E389", {"start": v(29.99, 26.51) * mm, "end": v(42.16, 26.51) * mm});
            skLineSegment(sketch, "E390", {"start": v(42.16, 26.51) * mm, "end": v(42.16, 19.81) * mm});
            skLineSegment(sketch, "E391", {"start": v(42.16, 19.81) * mm, "end": v(42.16, 13.1) * mm});
            skLineSegment(sketch, "E392", {"start": v(42.16, 13.1) * mm, "end": v(40.92, 13.1) * mm});
            skFitSpline(sketch, "E393", {"points": [v(40.92, 13.1) * mm, v(40.24, 13.1) * mm, v(39.69, 13.02) * mm, v(39.69, 12.92) * mm]});
            skFitSpline(sketch, "E394", {"points": [v(39.69, 12.92) * mm, v(39.69, 12.77) * mm, v(41.33, 7.1) * mm, v(42.01, 4.9) * mm]});
            skFitSpline(sketch, "E395", {"points": [v(42.01, 4.9) * mm, v(42.18, 4.36) * mm, v(41.93, 4.29) * mm, v(39.75, 4.29) * mm]});
            skLineSegment(sketch, "E396", {"start": v(39.75, 4.29) * mm, "end": v(37.29, 4.29) * mm});
            skLineSegment(sketch, "E397", {"start": v(37.29, 4.29) * mm, "end": v(36.52, 6.85) * mm});
            skFitSpline(sketch, "E398", {"points": [v(36.52, 6.85) * mm, v(36.1, 8.25) * mm, v(35.5, 10.24) * mm, v(35.19, 11.26) * mm]});
            skLineSegment(sketch, "E399", {"start": v(35.19, 11.26) * mm, "end": v(34.62, 13.1) * mm});
            skLineSegment(sketch, "E400", {"start": v(34.62, 13.1) * mm, "end": v(28.51, 13.1) * mm});
            skLineSegment(sketch, "E401", {"start": v(28.51, 13.1) * mm, "end": v(22.4, 13.1) * mm});
            skLineSegment(sketch, "E402", {"start": v(22.4, 13.1) * mm, "end": v(22.4, 8.7) * mm});
            skLineSegment(sketch, "E403", {"start": v(22.4, 8.7) * mm, "end": v(22.4, 4.29) * mm});
            skLineSegment(sketch, "E404", {"start": v(22.4, 4.29) * mm, "end": v(20.1, 4.29) * mm});
            skLineSegment(sketch, "E405", {"start": v(20.1, 4.29) * mm, "end": v(17.82, 4.29) * mm});
            skLineSegment(sketch, "E406", {"start": v(17.82, 4.29) * mm, "end": v(17.82, 15.4) * mm});
            skLineSegment(sketch, "E407", {"start": v(37.57, 19.81) * mm, "end": v(37.57, 21.93) * mm});
            skLineSegment(sketch, "E408", {"start": v(37.57, 21.93) * mm, "end": v(29.99, 21.93) * mm});
            skLineSegment(sketch, "E409", {"start": v(29.99, 21.93) * mm, "end": v(22.4, 21.93) * mm});
            skLineSegment(sketch, "E410", {"start": v(22.4, 21.93) * mm, "end": v(22.4, 19.81) * mm});
            skLineSegment(sketch, "E411", {"start": v(22.4, 19.81) * mm, "end": v(22.4, 17.7) * mm});
            skLineSegment(sketch, "E412", {"start": v(22.4, 17.7) * mm, "end": v(29.99, 17.7) * mm});
            skLineSegment(sketch, "E413", {"start": v(29.99, 17.7) * mm, "end": v(37.57, 17.7) * mm});
            skLineSegment(sketch, "E414", {"start": v(37.57, 17.7) * mm, "end": v(37.57, 19.81) * mm});
            skLineSegment(sketch, "E415", {"start": v(46.04, 15.4) * mm, "end": v(46.04, 26.51) * mm});
            skLineSegment(sketch, "E416", {"start": v(46.04, 26.51) * mm, "end": v(48.5, 26.51) * mm});
            skLineSegment(sketch, "E417", {"start": v(48.5, 26.51) * mm, "end": v(50.98, 26.51) * mm});
            skLineSegment(sketch, "E418", {"start": v(50.98, 26.51) * mm, "end": v(50.98, 15.4) * mm});
            skLineSegment(sketch, "E419", {"start": v(50.98, 15.4) * mm, "end": v(50.98, 4.29) * mm});
            skLineSegment(sketch, "E420", {"start": v(50.98, 4.29) * mm, "end": v(48.5, 4.29) * mm});
            skLineSegment(sketch, "E421", {"start": v(48.5, 4.29) * mm, "end": v(46.04, 4.29) * mm});
            skLineSegment(sketch, "E422", {"start": v(46.04, 4.29) * mm, "end": v(46.04, 15.4) * mm});
            skLineSegment(sketch, "E423", {"start": v(54.86, 15.4) * mm, "end": v(54.86, 26.51) * mm});
            skLineSegment(sketch, "E424", {"start": v(54.86, 26.51) * mm, "end": v(67.2, 26.51) * mm});
            skLineSegment(sketch, "E425", {"start": v(67.2, 26.51) * mm, "end": v(79.55, 26.51) * mm});
            skLineSegment(sketch, "E426", {"start": v(79.55, 26.51) * mm, "end": v(79.55, 24.22) * mm});
            skLineSegment(sketch, "E427", {"start": v(79.55, 24.22) * mm, "end": v(79.55, 21.93) * mm});
            skLineSegment(sketch, "E428", {"start": v(79.55, 21.93) * mm, "end": v(69.67, 21.93) * mm});
            skLineSegment(sketch, "E429", {"start": v(69.67, 21.93) * mm, "end": v(59.8, 21.93) * mm});
            skLineSegment(sketch, "E430", {"start": v(59.8, 21.93) * mm, "end": v(59.8, 19.81) * mm});
            skLineSegment(sketch, "E431", {"start": v(59.8, 19.81) * mm, "end": v(59.8, 17.7) * mm});
            skLineSegment(sketch, "E432", {"start": v(59.8, 17.7) * mm, "end": v(69.67, 17.7) * mm});
            skLineSegment(sketch, "E433", {"start": v(69.67, 17.7) * mm, "end": v(79.55, 17.7) * mm});
            skLineSegment(sketch, "E434", {"start": v(79.55, 17.7) * mm, "end": v(79.55, 15.4) * mm});
            skLineSegment(sketch, "E435", {"start": v(79.55, 15.4) * mm, "end": v(79.55, 13.1) * mm});
            skLineSegment(sketch, "E436", {"start": v(79.55, 13.1) * mm, "end": v(69.67, 13.1) * mm});
            skLineSegment(sketch, "E437", {"start": v(69.67, 13.1) * mm, "end": v(59.8, 13.1) * mm});
            skLineSegment(sketch, "E438", {"start": v(59.8, 13.1) * mm, "end": v(59.8, 10.82) * mm});
            skLineSegment(sketch, "E439", {"start": v(59.8, 10.82) * mm, "end": v(59.8, 8.52) * mm});
            skLineSegment(sketch, "E440", {"start": v(59.8, 8.52) * mm, "end": v(69.67, 8.52) * mm});
            skLineSegment(sketch, "E441", {"start": v(69.67, 8.52) * mm, "end": v(79.55, 8.52) * mm});
            skLineSegment(sketch, "E442", {"start": v(79.55, 8.52) * mm, "end": v(79.55, 6.4) * mm});
            skLineSegment(sketch, "E443", {"start": v(79.55, 6.4) * mm, "end": v(79.55, 4.29) * mm});
            skLineSegment(sketch, "E444", {"start": v(79.55, 4.29) * mm, "end": v(67.2, 4.29) * mm});
            skLineSegment(sketch, "E445", {"start": v(67.2, 4.29) * mm, "end": v(54.86, 4.29) * mm});
            skLineSegment(sketch, "E446", {"start": v(54.86, 4.29) * mm, "end": v(54.86, 15.4) * mm});
            skLineSegment(sketch, "E447", {"start": v(83.43, 15.4) * mm, "end": v(83.43, 26.51) * mm});
            skLineSegment(sketch, "E448", {"start": v(83.43, 26.51) * mm, "end": v(95.78, 26.51) * mm});
            skLineSegment(sketch, "E449", {"start": v(95.78, 26.51) * mm, "end": v(108.13, 26.51) * mm});
            skLineSegment(sketch, "E450", {"start": v(108.13, 26.51) * mm, "end": v(108.13, 15.4) * mm});
            skLineSegment(sketch, "E451", {"start": v(108.13, 15.4) * mm, "end": v(108.13, 4.29) * mm});
            skLineSegment(sketch, "E452", {"start": v(108.13, 4.29) * mm, "end": v(105.66, 4.29) * mm});
            skLineSegment(sketch, "E453", {"start": v(105.66, 4.29) * mm, "end": v(103.19, 4.29) * mm});
            skLineSegment(sketch, "E454", {"start": v(103.19, 4.29) * mm, "end": v(103.19, 13.1) * mm});
            skLineSegment(sketch, "E455", {"start": v(103.19, 13.1) * mm, "end": v(103.19, 21.93) * mm});
            skLineSegment(sketch, "E456", {"start": v(103.19, 21.93) * mm, "end": v(95.78, 21.93) * mm});
            skLineSegment(sketch, "E457", {"start": v(95.78, 21.93) * mm, "end": v(88.37, 21.93) * mm});
            skLineSegment(sketch, "E458", {"start": v(88.37, 21.93) * mm, "end": v(88.37, 13.1) * mm});
            skLineSegment(sketch, "E459", {"start": v(88.37, 13.1) * mm, "end": v(88.37, 4.29) * mm});
            skLineSegment(sketch, "E460", {"start": v(88.37, 4.29) * mm, "end": v(85.9, 4.29) * mm});
            skLineSegment(sketch, "E461", {"start": v(85.9, 4.29) * mm, "end": v(83.43, 4.29) * mm});
            skLineSegment(sketch, "E462", {"start": v(83.43, 4.29) * mm, "end": v(83.43, 15.4) * mm});
            skLineSegment(sketch, "E463", {"start": v(112, 15.4) * mm, "end": v(112, 26.51) * mm});
            skLineSegment(sketch, "E464", {"start": v(112, 26.51) * mm, "end": v(124.18, 26.51) * mm});
            skLineSegment(sketch, "E465", {"start": v(124.18, 26.51) * mm, "end": v(136.35, 26.51) * mm});
            skLineSegment(sketch, "E466", {"start": v(136.35, 26.51) * mm, "end": v(136.35, 24.22) * mm});
            skLineSegment(sketch, "E467", {"start": v(136.35, 24.22) * mm, "end": v(136.35, 21.93) * mm});
            skLineSegment(sketch, "E468", {"start": v(136.35, 21.93) * mm, "end": v(126.47, 21.93) * mm});
            skLineSegment(sketch, "E469", {"start": v(126.47, 21.93) * mm, "end": v(116.6, 21.93) * mm});
            skLineSegment(sketch, "E470", {"start": v(116.6, 21.93) * mm, "end": v(116.6, 15.22) * mm});
            skLineSegment(sketch, "E471", {"start": v(116.6, 15.22) * mm, "end": v(116.6, 8.52) * mm});
            skLineSegment(sketch, "E472", {"start": v(116.6, 8.52) * mm, "end": v(126.47, 8.52) * mm});
            skLineSegment(sketch, "E473", {"start": v(126.47, 8.52) * mm, "end": v(136.35, 8.52) * mm});
            skLineSegment(sketch, "E474", {"start": v(136.35, 8.52) * mm, "end": v(136.35, 6.4) * mm});
            skLineSegment(sketch, "E475", {"start": v(136.35, 6.4) * mm, "end": v(136.35, 4.29) * mm});
            skLineSegment(sketch, "E476", {"start": v(136.35, 4.29) * mm, "end": v(124.18, 4.29) * mm});
            skLineSegment(sketch, "E477", {"start": v(124.18, 4.29) * mm, "end": v(112, 4.29) * mm});
            skLineSegment(sketch, "E478", {"start": v(112, 4.29) * mm, "end": v(112, 15.4) * mm});
            skLineSegment(sketch, "E479", {"start": v(140.58, 15.4) * mm, "end": v(140.58, 26.51) * mm});
            skLineSegment(sketch, "E480", {"start": v(140.58, 26.51) * mm, "end": v(152.75, 26.51) * mm});
            skLineSegment(sketch, "E481", {"start": v(152.75, 26.51) * mm, "end": v(164.92, 26.51) * mm});
            skLineSegment(sketch, "E482", {"start": v(164.92, 26.51) * mm, "end": v(164.92, 24.22) * mm});
            skLineSegment(sketch, "E483", {"start": v(164.92, 24.22) * mm, "end": v(164.92, 21.93) * mm});
            skLineSegment(sketch, "E484", {"start": v(164.92, 21.93) * mm, "end": v(155.05, 21.93) * mm});
            skLineSegment(sketch, "E485", {"start": v(155.05, 21.93) * mm, "end": v(145.17, 21.93) * mm});
            skLineSegment(sketch, "E486", {"start": v(145.17, 21.93) * mm, "end": v(145.17, 19.81) * mm});
            skLineSegment(sketch, "E487", {"start": v(145.17, 19.81) * mm, "end": v(145.17, 17.7) * mm});
            skLineSegment(sketch, "E488", {"start": v(145.17, 17.7) * mm, "end": v(155.05, 17.7) * mm});
            skLineSegment(sketch, "E489", {"start": v(155.05, 17.7) * mm, "end": v(164.92, 17.7) * mm});
            skLineSegment(sketch, "E490", {"start": v(164.92, 17.7) * mm, "end": v(164.92, 15.4) * mm});
            skLineSegment(sketch, "E491", {"start": v(164.92, 15.4) * mm, "end": v(164.92, 13.1) * mm});
            skLineSegment(sketch, "E492", {"start": v(164.92, 13.1) * mm, "end": v(155.05, 13.1) * mm});
            skLineSegment(sketch, "E493", {"start": v(155.05, 13.1) * mm, "end": v(145.17, 13.1) * mm});
            skLineSegment(sketch, "E494", {"start": v(145.17, 13.1) * mm, "end": v(145.17, 10.82) * mm});
            skLineSegment(sketch, "E495", {"start": v(145.17, 10.82) * mm, "end": v(145.17, 8.52) * mm});
            skLineSegment(sketch, "E496", {"start": v(145.17, 8.52) * mm, "end": v(155.05, 8.52) * mm});
            skLineSegment(sketch, "E497", {"start": v(155.05, 8.52) * mm, "end": v(164.92, 8.52) * mm});
            skLineSegment(sketch, "E498", {"start": v(164.92, 8.52) * mm, "end": v(164.92, 6.4) * mm});
            skLineSegment(sketch, "E499", {"start": v(164.92, 6.4) * mm, "end": v(164.92, 4.29) * mm});
            skLineSegment(sketch, "E500", {"start": v(164.92, 4.29) * mm, "end": v(152.75, 4.29) * mm});
            skLineSegment(sketch, "E501", {"start": v(152.75, 4.29) * mm, "end": v(140.58, 4.29) * mm});
            skLineSegment(sketch, "E502", {"start": v(140.58, 4.29) * mm, "end": v(140.58, 15.4) * mm});
            skLineSegment(sketch, "E503", {"start": v(169.16, 6.4) * mm, "end": v(169.16, 8.52) * mm});
            skLineSegment(sketch, "E504", {"start": v(169.16, 8.52) * mm, "end": v(179.03, 8.52) * mm});
            skLineSegment(sketch, "E505", {"start": v(179.03, 8.52) * mm, "end": v(188.91, 8.52) * mm});
            skLineSegment(sketch, "E506", {"start": v(188.91, 8.52) * mm, "end": v(188.91, 10.82) * mm});
            skLineSegment(sketch, "E507", {"start": v(188.91, 10.82) * mm, "end": v(188.91, 13.1) * mm});
            skLineSegment(sketch, "E508", {"start": v(188.91, 13.1) * mm, "end": v(179.03, 13.1) * mm});
            skLineSegment(sketch, "E509", {"start": v(179.03, 13.1) * mm, "end": v(169.16, 13.1) * mm});
            skLineSegment(sketch, "E510", {"start": v(169.16, 13.1) * mm, "end": v(169.16, 19.81) * mm});
            skLineSegment(sketch, "E511", {"start": v(169.16, 19.81) * mm, "end": v(169.16, 26.51) * mm});
            skLineSegment(sketch, "E512", {"start": v(169.16, 26.51) * mm, "end": v(181.33, 26.51) * mm});
            skLineSegment(sketch, "E513", {"start": v(181.33, 26.51) * mm, "end": v(193.5, 26.51) * mm});
            skLineSegment(sketch, "E514", {"start": v(193.5, 26.51) * mm, "end": v(193.5, 24.22) * mm});
            skLineSegment(sketch, "E515", {"start": v(193.5, 24.22) * mm, "end": v(193.5, 21.93) * mm});
            skLineSegment(sketch, "E516", {"start": v(193.5, 21.93) * mm, "end": v(183.62, 21.93) * mm});
            skLineSegment(sketch, "E517", {"start": v(183.62, 21.93) * mm, "end": v(173.74, 21.93) * mm});
            skLineSegment(sketch, "E518", {"start": v(173.74, 21.93) * mm, "end": v(173.74, 19.81) * mm});
            skLineSegment(sketch, "E519", {"start": v(173.74, 19.81) * mm, "end": v(173.74, 17.7) * mm});
            skLineSegment(sketch, "E520", {"start": v(173.74, 17.7) * mm, "end": v(183.62, 17.7) * mm});
            skLineSegment(sketch, "E521", {"start": v(183.62, 17.7) * mm, "end": v(193.5, 17.7) * mm});
            skLineSegment(sketch, "E522", {"start": v(193.5, 17.7) * mm, "end": v(193.5, 11) * mm});
            skLineSegment(sketch, "E523", {"start": v(193.5, 11) * mm, "end": v(193.5, 4.29) * mm});
            skLineSegment(sketch, "E524", {"start": v(193.5, 4.29) * mm, "end": v(181.33, 4.29) * mm});
            skLineSegment(sketch, "E525", {"start": v(181.33, 4.29) * mm, "end": v(169.16, 4.29) * mm});
            skLineSegment(sketch, "E526", {"start": v(169.16, 4.29) * mm, "end": v(169.16, 6.4) * mm});
            skLineSegment(sketch, "E527", {"start": v(-75.67, 41.5) * mm, "end": v(-75.67, 43.1) * mm});
            skLineSegment(sketch, "E528", {"start": v(-75.67, 43.1) * mm, "end": v(62.8, 43.1) * mm});
            skLineSegment(sketch, "E529", {"start": v(62.8, 43.1) * mm, "end": v(201.26, 43.1) * mm});
            skLineSegment(sketch, "E530", {"start": v(201.26, 43.1) * mm, "end": v(201.26, 41.5) * mm});
            skLineSegment(sketch, "E531", {"start": v(201.26, 41.5) * mm, "end": v(201.26, 39.92) * mm});
            skLineSegment(sketch, "E532", {"start": v(201.26, 39.92) * mm, "end": v(62.8, 39.92) * mm});
            skLineSegment(sketch, "E533", {"start": v(62.8, 39.92) * mm, "end": v(-75.67, 39.92) * mm});
            skLineSegment(sketch, "E534", {"start": v(-75.67, 39.92) * mm, "end": v(-75.67, 41.5) * mm});
            skLineSegment(sketch, "E535.bottom", {"start": v(247.67, 69.49) * mm, "end": v(-247.67, 69.49) * mm});
            skLineSegment(sketch, "E535.top", {"start": v(247.67, -69.49) * mm, "end": v(-247.67, -69.49) * mm});
            skLineSegment(sketch, "E535.left", {"start": v(247.67, 69.49) * mm, "end": v(247.67, -69.49) * mm});
            skLineSegment(sketch, "E535.right", {"start": v(-247.67, 69.49) * mm, "end": v(-247.67, -69.49) * mm});
            skPoint(sketch, "E535.middle", {"position": v(0, 0) * mm});
            skSolve(sketch);
        }
        {
            var Q0;
            Q0=makeQuery(id+"F0.imprint","IMPRINT",FACE,{"disambiguationData":[TD([[makeQuery(id+"F0.imprint","IMPRINT",EDGE,{"derivedFrom":sQuery(id+"F0.wireOp",EDGE,"E289")}),-1.0]])]});
            var Q1;
            Q1=makeQuery(id+"F0.imprint","IMPRINT",FACE,{"disambiguationData":[TD([[makeQuery(id+"F0.imprint","IMPRINT",EDGE,{"derivedFrom":sQuery(id+"F0.wireOp",EDGE,"E363")}),-1.0]])]});
            var Q2;
            Q2=makeQuery(id+"F0.imprint","IMPRINT",FACE,{"disambiguationData":[TD([[makeQuery(id+"F0.imprint","IMPRINT",EDGE,{"derivedFrom":sQuery(id+"F0.wireOp",EDGE,"E415")}),-1.0]])]});
            var Q3;
            Q3=makeQuery(id+"F0.imprint","IMPRINT",FACE,{"disambiguationData":[TD([[makeQuery(id+"F0.imprint","IMPRINT",EDGE,{"derivedFrom":sQuery(id+"F0.wireOp",EDGE,"E423")}),-1.0]])]});
            var Q4;
            Q4=makeQuery(id+"F0.imprint","IMPRINT",FACE,{"disambiguationData":[TD([[makeQuery(id+"F0.imprint","IMPRINT",EDGE,{"derivedFrom":sQuery(id+"F0.wireOp",EDGE,"E479")}),-1.0]])]});
            var Q5;
            Q5=makeQuery(id+"F0.imprint","IMPRINT",FACE,{"disambiguationData":[TD([[makeQuery(id+"F0.imprint","IMPRINT",EDGE,{"derivedFrom":sQuery(id+"F0.wireOp",EDGE,"E55")}),-1.0]])]});
            var Q6;
            Q6=makeQuery(id+"F0.imprint","IMPRINT",FACE,{"disambiguationData":[TD([[makeQuery(id+"F0.imprint","IMPRINT",EDGE,{"derivedFrom":sQuery(id+"F0.wireOp",EDGE,"E199")}),-1.0]])]});
            var Q7;
            Q7=makeQuery(id+"F0.imprint","IMPRINT",FACE,{"disambiguationData":[TD([[makeQuery(id+"F0.imprint","IMPRINT",EDGE,{"derivedFrom":sQuery(id+"F0.wireOp",EDGE,"E207")}),-1.0]])]});
            var Q8;
            Q8=makeQuery(id+"F0.imprint","IMPRINT",FACE,{"disambiguationData":[TD([[makeQuery(id+"F0.imprint","IMPRINT",EDGE,{"derivedFrom":sQuery(id+"F0.wireOp",EDGE,"E151")}),-1.0]])]});
            var Q9;
            Q9=makeQuery(id+"F0.imprint","IMPRINT",FACE,{"disambiguationData":[TD([[makeQuery(id+"F0.imprint","IMPRINT",EDGE,{"derivedFrom":sQuery(id+"F0.wireOp",EDGE,"E163")}),-1.0]])]});
            var Q10;
            Q10=makeQuery(id+"F0.imprint","IMPRINT",FACE,{"disambiguationData":[TD([[makeQuery(id+"F0.imprint","IMPRINT",EDGE,{"derivedFrom":sQuery(id+"F0.wireOp",EDGE,"E447")}),-1.0]])]});
            var Q11;
            Q11=makeQuery(id+"F0.imprint","IMPRINT",FACE,{"disambiguationData":[TD([[makeQuery(id+"F0.imprint","IMPRINT",EDGE,{"derivedFrom":sQuery(id+"F0.wireOp",EDGE,"E463")}),-1.0]])]});
            var Q12;
            Q12=makeQuery(id+"F0.imprint","IMPRINT",FACE,{"disambiguationData":[TD([[makeQuery(id+"F0.imprint","IMPRINT",EDGE,{"derivedFrom":sQuery(id+"F0.wireOp",EDGE,"E503")}),-1.0]])]});
            var Q13;
            Q13=makeQuery(id+"F0.imprint","IMPRINT",FACE,{"disambiguationData":[TD([[makeQuery(id+"F0.imprint","IMPRINT",EDGE,{"derivedFrom":sQuery(id+"F0.wireOp",EDGE,"E527")}),-1.0]])]});
            var Q14;
            Q14=makeQuery(id+"F0.imprint","IMPRINT",FACE,{"disambiguationData":[TD([[makeQuery(id+"F0.imprint","IMPRINT",EDGE,{"derivedFrom":sQuery(id+"F0.wireOp",EDGE,"E135")}),-1.0]])]});
            var Q15;
            Q15=makeQuery(id+"F0.imprint","IMPRINT",FACE,{"disambiguationData":[TD([[makeQuery(id+"F0.imprint","IMPRINT",EDGE,{"derivedFrom":sQuery(id+"F0.wireOp",EDGE,"E231")}),-1.0]])]});
            var Q16;
            Q16=makeQuery(id+"F0.imprint","IMPRINT",FACE,{"disambiguationData":[TD([[makeQuery(id+"F0.imprint","IMPRINT",EDGE,{"derivedFrom":sQuery(id+"F0.wireOp",EDGE,"E31")}),-1.0]])]});
            var Q17;
            Q17=makeQuery(id+"F0.imprint","IMPRINT",FACE,{"disambiguationData":[TD([[makeQuery(id+"F0.imprint","IMPRINT",EDGE,{"derivedFrom":sQuery(id+"F0.wireOp",EDGE,"E39")}),-1.0]])]});
            var Q18;
            Q18=makeQuery(id+"F0.imprint","IMPRINT",FACE,{"disambiguationData":[TD([[makeQuery(id+"F0.imprint","IMPRINT",EDGE,{"derivedFrom":sQuery(id+"F0.wireOp",EDGE,"E179")}),-1.0]])]});
            var Q19;
            Q19=makeQuery(id+"F0.imprint","IMPRINT",FACE,{"disambiguationData":[TD([[makeQuery(id+"F0.imprint","IMPRINT",EDGE,{"derivedFrom":sQuery(id+"F0.wireOp",EDGE,"E79")}),-1.0]])]});
            var Q20;
            Q20=makeQuery(id+"F0.imprint","IMPRINT",FACE,{"disambiguationData":[TD([[makeQuery(id+"F0.imprint","IMPRINT",EDGE,{"derivedFrom":sQuery(id+"F0.wireOp",EDGE,"E95")}),-1.0]])]});
            var Q21;
            Q21=makeQuery(id+"F0.imprint","IMPRINT",FACE,{"disambiguationData":[TD([[makeQuery(id+"F0.imprint","IMPRINT",EDGE,{"derivedFrom":sQuery(id+"F0.wireOp",EDGE,"E343")}),-1.0]])]});
            var Q22;
            Q22=makeQuery(id+"F0.imprint","IMPRINT",FACE,{"disambiguationData":[TD([[makeQuery(id+"F0.imprint","IMPRINT",EDGE,{"derivedFrom":sQuery(id+"F0.wireOp",EDGE,"E387")}),-1.0]])]});
            var Q23;
            Q23=makeQuery(id+"F0.imprint","IMPRINT",FACE,{"disambiguationData":[TD([[makeQuery(id+"F0.imprint","IMPRINT",EDGE,{"derivedFrom":sQuery(id+"F0.wireOp",EDGE,"E313")}),-1.0]])]});
            var Q24;
            Q24=makeQuery(id+"F0.imprint","IMPRINT",FACE,{"disambiguationData":[TD([[makeQuery(id+"F0.imprint","IMPRINT",EDGE,{"derivedFrom":sQuery(id+"F0.wireOp",EDGE,"E119")}),-1.0]])]});
            var Q25;
            Q25=makeQuery(id+"F0.imprint","IMPRINT",FACE,{"disambiguationData":[TD([[makeQuery(id+"F0.imprint","IMPRINT",EDGE,{"derivedFrom":sQuery(id+"F0.wireOp",EDGE,"E261")}),-1.0]])]});
            extrude(context, id + "F1", {"entities" : qUnion([Q0, Q1, Q2, Q3, Q4, Q5, Q6, Q7, Q8, Q9, Q10, Q11, Q12, Q13, Q14, Q15, Q16, Q17, Q18, Q19, Q20, Q21, Q22, Q23, Q24, Q25]), "depth" : 8 * mm});
        }
        {
            var Q0;
            Q0=qCreatedBy(makeId("Front.planeOp"),FACE);
            var sketch = newSketch(context, id + "F2", { "sketchPlane" : qUnion([Q0])});
            skLineSegment(sketch, "E536.0", {"start": v(247.67, 69.49) * mm, "end": v(-247.67, 69.49) * mm});
            skLineSegment(sketch, "E537.0", {"start": v(247.67, 69.49) * mm, "end": v(247.67, -69.49) * mm});
            skLineSegment(sketch, "E538.0", {"start": v(247.67, -69.49) * mm, "end": v(-247.67, -69.49) * mm});
            skLineSegment(sketch, "E539.0", {"start": v(-247.67, 69.49) * mm, "end": v(-247.67, -69.49) * mm});
            skSolve(sketch);
        }
        {
            var Q0;
            Q0 = qSketchRegion(id + "F2", true);
            extrude(context, id + "F3", {"entities" : qUnion([Q0]), "oppositeDirection" : true, "depth" : 6 * mm});
        }
        {
            var Q0;
            Q0=makeQuery(id+"F0.imprint","IMPRINT",FACE,{"disambiguationData":[TD([[makeQuery(id+"F0.imprint","IMPRINT",EDGE,{"derivedFrom":sQuery(id+"F0.wireOp",EDGE,"E0")}),-1.0]])]});
            var Q1;
            Q1=makeQuery(id+"F0.imprint","IMPRINT",FACE,{"disambiguationData":[TD([[makeQuery(id+"F0.imprint","IMPRINT",EDGE,{"derivedFrom":sQuery(id+"F0.wireOp",EDGE,"E255")}),-1.0]])]});
            extrude(context, id + "F4", {"entities" : qUnion([Q0, Q1]), "depth" : 25 * mm});
        }
        {
            var Q0;
            Q0=makeQuery(id+"F1.opExtrude","SWEPT_BODY",BODY,{"disambiguationData":[OSD([sQuery(id+"F0.wireOp",EDGE,"E503"),sQuery(id+"F0.wireOp",EDGE,"E504"),sQuery(id+"F0.wireOp",EDGE,"E505"),sQuery(id+"F0.wireOp",EDGE,"E506"),sQuery(id+"F0.wireOp",EDGE,"E507"),sQuery(id+"F0.wireOp",EDGE,"E508"),sQuery(id+"F0.wireOp",EDGE,"E509"),sQuery(id+"F0.wireOp",EDGE,"E510"),sQuery(id+"F0.wireOp",EDGE,"E511"),sQuery(id+"F0.wireOp",EDGE,"E512"),sQuery(id+"F0.wireOp",EDGE,"E513"),sQuery(id+"F0.wireOp",EDGE,"E514"),sQuery(id+"F0.wireOp",EDGE,"E515"),sQuery(id+"F0.wireOp",EDGE,"E516"),sQuery(id+"F0.wireOp",EDGE,"E517"),sQuery(id+"F0.wireOp",EDGE,"E518"),sQuery(id+"F0.wireOp",EDGE,"E519"),sQuery(id+"F0.wireOp",EDGE,"E520"),sQuery(id+"F0.wireOp",EDGE,"E521"),sQuery(id+"F0.wireOp",EDGE,"E522"),sQuery(id+"F0.wireOp",EDGE,"E523"),sQuery(id+"F0.wireOp",EDGE,"E524"),sQuery(id+"F0.wireOp",EDGE,"E525"),sQuery(id+"F0.wireOp",EDGE,"E526")])]});
            var Q1;
            Q1=makeQuery(id+"F1.opExtrude","SWEPT_BODY",BODY,{"disambiguationData":[OSD([sQuery(id+"F0.wireOp",EDGE,"E527"),sQuery(id+"F0.wireOp",EDGE,"E528"),sQuery(id+"F0.wireOp",EDGE,"E529"),sQuery(id+"F0.wireOp",EDGE,"E530"),sQuery(id+"F0.wireOp",EDGE,"E531"),sQuery(id+"F0.wireOp",EDGE,"E532"),sQuery(id+"F0.wireOp",EDGE,"E533"),sQuery(id+"F0.wireOp",EDGE,"E534")])]});
            var Q2;
            Q2=makeQuery(id+"F3.opExtrude","SWEPT_BODY",BODY,{"disambiguationData":[OSD([sQuery(id+"F2.wireOp",EDGE,"E536.0"),sQuery(id+"F2.wireOp",EDGE,"E537.0"),sQuery(id+"F2.wireOp",EDGE,"E538.0"),sQuery(id+"F2.wireOp",EDGE,"E539.0")])]});
            var Q3;
            Q3=makeQuery(id+"F1.opExtrude","SWEPT_BODY",BODY,{"disambiguationData":[OSD([sQuery(id+"F0.wireOp",EDGE,"E463"),sQuery(id+"F0.wireOp",EDGE,"E464"),sQuery(id+"F0.wireOp",EDGE,"E465"),sQuery(id+"F0.wireOp",EDGE,"E466"),sQuery(id+"F0.wireOp",EDGE,"E467"),sQuery(id+"F0.wireOp",EDGE,"E468"),sQuery(id+"F0.wireOp",EDGE,"E469"),sQuery(id+"F0.wireOp",EDGE,"E470"),sQuery(id+"F0.wireOp",EDGE,"E471"),sQuery(id+"F0.wireOp",EDGE,"E472"),sQuery(id+"F0.wireOp",EDGE,"E473"),sQuery(id+"F0.wireOp",EDGE,"E474"),sQuery(id+"F0.wireOp",EDGE,"E475"),sQuery(id+"F0.wireOp",EDGE,"E476"),sQuery(id+"F0.wireOp",EDGE,"E477"),sQuery(id+"F0.wireOp",EDGE,"E478")])]});
            var Q4;
            Q4=makeQuery(id+"F1.opExtrude","SWEPT_BODY",BODY,{"disambiguationData":[OSD([sQuery(id+"F0.wireOp",EDGE,"E479"),sQuery(id+"F0.wireOp",EDGE,"E480"),sQuery(id+"F0.wireOp",EDGE,"E481"),sQuery(id+"F0.wireOp",EDGE,"E482"),sQuery(id+"F0.wireOp",EDGE,"E483"),sQuery(id+"F0.wireOp",EDGE,"E484"),sQuery(id+"F0.wireOp",EDGE,"E485"),sQuery(id+"F0.wireOp",EDGE,"E486"),sQuery(id+"F0.wireOp",EDGE,"E487"),sQuery(id+"F0.wireOp",EDGE,"E488"),sQuery(id+"F0.wireOp",EDGE,"E489"),sQuery(id+"F0.wireOp",EDGE,"E490"),sQuery(id+"F0.wireOp",EDGE,"E491"),sQuery(id+"F0.wireOp",EDGE,"E492"),sQuery(id+"F0.wireOp",EDGE,"E493"),sQuery(id+"F0.wireOp",EDGE,"E494"),sQuery(id+"F0.wireOp",EDGE,"E495"),sQuery(id+"F0.wireOp",EDGE,"E496"),sQuery(id+"F0.wireOp",EDGE,"E497"),sQuery(id+"F0.wireOp",EDGE,"E498"),sQuery(id+"F0.wireOp",EDGE,"E499"),sQuery(id+"F0.wireOp",EDGE,"E500"),sQuery(id+"F0.wireOp",EDGE,"E501"),sQuery(id+"F0.wireOp",EDGE,"E502")])]});
            var Q5;
            Q5=makeQuery(id+"F1.opExtrude","SWEPT_BODY",BODY,{"disambiguationData":[OSD([sQuery(id+"F0.wireOp",EDGE,"E447"),sQuery(id+"F0.wireOp",EDGE,"E448"),sQuery(id+"F0.wireOp",EDGE,"E449"),sQuery(id+"F0.wireOp",EDGE,"E450"),sQuery(id+"F0.wireOp",EDGE,"E451"),sQuery(id+"F0.wireOp",EDGE,"E452"),sQuery(id+"F0.wireOp",EDGE,"E453"),sQuery(id+"F0.wireOp",EDGE,"E454"),sQuery(id+"F0.wireOp",EDGE,"E455"),sQuery(id+"F0.wireOp",EDGE,"E456"),sQuery(id+"F0.wireOp",EDGE,"E457"),sQuery(id+"F0.wireOp",EDGE,"E458"),sQuery(id+"F0.wireOp",EDGE,"E459"),sQuery(id+"F0.wireOp",EDGE,"E460"),sQuery(id+"F0.wireOp",EDGE,"E461"),sQuery(id+"F0.wireOp",EDGE,"E462")])]});
            var Q6;
            Q6=makeQuery(id+"F1.opExtrude","SWEPT_BODY",BODY,{"disambiguationData":[OSD([sQuery(id+"F0.wireOp",EDGE,"E423"),sQuery(id+"F0.wireOp",EDGE,"E424"),sQuery(id+"F0.wireOp",EDGE,"E425"),sQuery(id+"F0.wireOp",EDGE,"E426"),sQuery(id+"F0.wireOp",EDGE,"E427"),sQuery(id+"F0.wireOp",EDGE,"E428"),sQuery(id+"F0.wireOp",EDGE,"E429"),sQuery(id+"F0.wireOp",EDGE,"E430"),sQuery(id+"F0.wireOp",EDGE,"E431"),sQuery(id+"F0.wireOp",EDGE,"E432"),sQuery(id+"F0.wireOp",EDGE,"E433"),sQuery(id+"F0.wireOp",EDGE,"E434"),sQuery(id+"F0.wireOp",EDGE,"E435"),sQuery(id+"F0.wireOp",EDGE,"E436"),sQuery(id+"F0.wireOp",EDGE,"E437"),sQuery(id+"F0.wireOp",EDGE,"E438"),sQuery(id+"F0.wireOp",EDGE,"E439"),sQuery(id+"F0.wireOp",EDGE,"E440"),sQuery(id+"F0.wireOp",EDGE,"E441"),sQuery(id+"F0.wireOp",EDGE,"E442"),sQuery(id+"F0.wireOp",EDGE,"E443"),sQuery(id+"F0.wireOp",EDGE,"E444"),sQuery(id+"F0.wireOp",EDGE,"E445"),sQuery(id+"F0.wireOp",EDGE,"E446")])]});
            var Q7;
            Q7=makeQuery(id+"F1.opExtrude","SWEPT_BODY",BODY,{"disambiguationData":[OSD([sQuery(id+"F0.wireOp",EDGE,"E415"),sQuery(id+"F0.wireOp",EDGE,"E416"),sQuery(id+"F0.wireOp",EDGE,"E417"),sQuery(id+"F0.wireOp",EDGE,"E418"),sQuery(id+"F0.wireOp",EDGE,"E419"),sQuery(id+"F0.wireOp",EDGE,"E420"),sQuery(id+"F0.wireOp",EDGE,"E421"),sQuery(id+"F0.wireOp",EDGE,"E422")])]});
            var Q8;
            Q8=makeQuery(id+"F1.opExtrude","SWEPT_BODY",BODY,{"disambiguationData":[OSD([sQuery(id+"F0.wireOp",EDGE,"E387"),sQuery(id+"F0.wireOp",EDGE,"E388"),sQuery(id+"F0.wireOp",EDGE,"E389"),sQuery(id+"F0.wireOp",EDGE,"E390"),sQuery(id+"F0.wireOp",EDGE,"E391"),sQuery(id+"F0.wireOp",EDGE,"E392"),sQuery(id+"F0.wireOp",EDGE,"E393"),sQuery(id+"F0.wireOp",EDGE,"E394"),sQuery(id+"F0.wireOp",EDGE,"E395"),sQuery(id+"F0.wireOp",EDGE,"E396"),sQuery(id+"F0.wireOp",EDGE,"E397"),sQuery(id+"F0.wireOp",EDGE,"E398"),sQuery(id+"F0.wireOp",EDGE,"E399"),sQuery(id+"F0.wireOp",EDGE,"E400"),sQuery(id+"F0.wireOp",EDGE,"E401"),sQuery(id+"F0.wireOp",EDGE,"E402"),sQuery(id+"F0.wireOp",EDGE,"E403"),sQuery(id+"F0.wireOp",EDGE,"E404"),sQuery(id+"F0.wireOp",EDGE,"E405"),sQuery(id+"F0.wireOp",EDGE,"E406"),sQuery(id+"F0.wireOp",EDGE,"E407"),sQuery(id+"F0.wireOp",EDGE,"E408"),sQuery(id+"F0.wireOp",EDGE,"E409"),sQuery(id+"F0.wireOp",EDGE,"E410"),sQuery(id+"F0.wireOp",EDGE,"E411"),sQuery(id+"F0.wireOp",EDGE,"E412"),sQuery(id+"F0.wireOp",EDGE,"E413"),sQuery(id+"F0.wireOp",EDGE,"E414")])]});
            var Q9;
            Q9=makeQuery(id+"F1.opExtrude","SWEPT_BODY",BODY,{"disambiguationData":[OSD([sQuery(id+"F0.wireOp",EDGE,"E313"),sQuery(id+"F0.wireOp",EDGE,"E314"),sQuery(id+"F0.wireOp",EDGE,"E315"),sQuery(id+"F0.wireOp",EDGE,"E316"),sQuery(id+"F0.wireOp",EDGE,"E317"),sQuery(id+"F0.wireOp",EDGE,"E318"),sQuery(id+"F0.wireOp",EDGE,"E319"),sQuery(id+"F0.wireOp",EDGE,"E320"),sQuery(id+"F0.wireOp",EDGE,"E321"),sQuery(id+"F0.wireOp",EDGE,"E322"),sQuery(id+"F0.wireOp",EDGE,"E323"),sQuery(id+"F0.wireOp",EDGE,"E324"),sQuery(id+"F0.wireOp",EDGE,"E325"),sQuery(id+"F0.wireOp",EDGE,"E326"),sQuery(id+"F0.wireOp",EDGE,"E327"),sQuery(id+"F0.wireOp",EDGE,"E328"),sQuery(id+"F0.wireOp",EDGE,"E329"),sQuery(id+"F0.wireOp",EDGE,"E330"),sQuery(id+"F0.wireOp",EDGE,"E331"),sQuery(id+"F0.wireOp",EDGE,"E332"),sQuery(id+"F0.wireOp",EDGE,"E333"),sQuery(id+"F0.wireOp",EDGE,"E334"),sQuery(id+"F0.wireOp",EDGE,"E335"),sQuery(id+"F0.wireOp",EDGE,"E336"),sQuery(id+"F0.wireOp",EDGE,"E337"),sQuery(id+"F0.wireOp",EDGE,"E338"),sQuery(id+"F0.wireOp",EDGE,"E339"),sQuery(id+"F0.wireOp",EDGE,"E340"),sQuery(id+"F0.wireOp",EDGE,"E341")])]});
            var Q10;
            Q10=makeQuery(id+"F1.opExtrude","SWEPT_BODY",BODY,{"disambiguationData":[OSD([sQuery(id+"F0.wireOp",EDGE,"E289"),sQuery(id+"F0.wireOp",EDGE,"E290"),sQuery(id+"F0.wireOp",EDGE,"E291"),sQuery(id+"F0.wireOp",EDGE,"E292"),sQuery(id+"F0.wireOp",EDGE,"E293"),sQuery(id+"F0.wireOp",EDGE,"E294"),sQuery(id+"F0.wireOp",EDGE,"E295"),sQuery(id+"F0.wireOp",EDGE,"E296"),sQuery(id+"F0.wireOp",EDGE,"E297"),sQuery(id+"F0.wireOp",EDGE,"E298"),sQuery(id+"F0.wireOp",EDGE,"E299"),sQuery(id+"F0.wireOp",EDGE,"E300"),sQuery(id+"F0.wireOp",EDGE,"E301"),sQuery(id+"F0.wireOp",EDGE,"E302"),sQuery(id+"F0.wireOp",EDGE,"E303"),sQuery(id+"F0.wireOp",EDGE,"E304"),sQuery(id+"F0.wireOp",EDGE,"E305"),sQuery(id+"F0.wireOp",EDGE,"E306"),sQuery(id+"F0.wireOp",EDGE,"E307"),sQuery(id+"F0.wireOp",EDGE,"E308"),sQuery(id+"F0.wireOp",EDGE,"E309"),sQuery(id+"F0.wireOp",EDGE,"E310"),sQuery(id+"F0.wireOp",EDGE,"E311"),sQuery(id+"F0.wireOp",EDGE,"E312")])]});
            var Q11;
            Q11=makeQuery(id+"F1.opExtrude","SWEPT_BODY",BODY,{"disambiguationData":[OSD([sQuery(id+"F0.wireOp",EDGE,"E261"),sQuery(id+"F0.wireOp",EDGE,"E262"),sQuery(id+"F0.wireOp",EDGE,"E263"),sQuery(id+"F0.wireOp",EDGE,"E264"),sQuery(id+"F0.wireOp",EDGE,"E265"),sQuery(id+"F0.wireOp",EDGE,"E266"),sQuery(id+"F0.wireOp",EDGE,"E267"),sQuery(id+"F0.wireOp",EDGE,"E268"),sQuery(id+"F0.wireOp",EDGE,"E269"),sQuery(id+"F0.wireOp",EDGE,"E270"),sQuery(id+"F0.wireOp",EDGE,"E271"),sQuery(id+"F0.wireOp",EDGE,"E272"),sQuery(id+"F0.wireOp",EDGE,"E273"),sQuery(id+"F0.wireOp",EDGE,"E274"),sQuery(id+"F0.wireOp",EDGE,"E275"),sQuery(id+"F0.wireOp",EDGE,"E276"),sQuery(id+"F0.wireOp",EDGE,"E277"),sQuery(id+"F0.wireOp",EDGE,"E278"),sQuery(id+"F0.wireOp",EDGE,"E279"),sQuery(id+"F0.wireOp",EDGE,"E280"),sQuery(id+"F0.wireOp",EDGE,"E281"),sQuery(id+"F0.wireOp",EDGE,"E282"),sQuery(id+"F0.wireOp",EDGE,"E283"),sQuery(id+"F0.wireOp",EDGE,"E284"),sQuery(id+"F0.wireOp",EDGE,"E285"),sQuery(id+"F0.wireOp",EDGE,"E286"),sQuery(id+"F0.wireOp",EDGE,"E287"),sQuery(id+"F0.wireOp",EDGE,"E288")])]});
            var Q12;
            Q12=makeQuery(id+"F1.opExtrude","SWEPT_BODY",BODY,{"disambiguationData":[OSD([sQuery(id+"F0.wireOp",EDGE,"E231"),sQuery(id+"F0.wireOp",EDGE,"E232"),sQuery(id+"F0.wireOp",EDGE,"E233"),sQuery(id+"F0.wireOp",EDGE,"E234"),sQuery(id+"F0.wireOp",EDGE,"E235"),sQuery(id+"F0.wireOp",EDGE,"E236"),sQuery(id+"F0.wireOp",EDGE,"E237"),sQuery(id+"F0.wireOp",EDGE,"E238"),sQuery(id+"F0.wireOp",EDGE,"E239"),sQuery(id+"F0.wireOp",EDGE,"E240"),sQuery(id+"F0.wireOp",EDGE,"E241"),sQuery(id+"F0.wireOp",EDGE,"E242"),sQuery(id+"F0.wireOp",EDGE,"E243"),sQuery(id+"F0.wireOp",EDGE,"E244"),sQuery(id+"F0.wireOp",EDGE,"E245"),sQuery(id+"F0.wireOp",EDGE,"E246"),sQuery(id+"F0.wireOp",EDGE,"E247"),sQuery(id+"F0.wireOp",EDGE,"E248"),sQuery(id+"F0.wireOp",EDGE,"E249"),sQuery(id+"F0.wireOp",EDGE,"E250"),sQuery(id+"F0.wireOp",EDGE,"E251"),sQuery(id+"F0.wireOp",EDGE,"E252"),sQuery(id+"F0.wireOp",EDGE,"E253"),sQuery(id+"F0.wireOp",EDGE,"E254")])]});
            var Q13;
            Q13=makeQuery(id+"F1.opExtrude","SWEPT_BODY",BODY,{"disambiguationData":[OSD([sQuery(id+"F0.wireOp",EDGE,"E207"),sQuery(id+"F0.wireOp",EDGE,"E208"),sQuery(id+"F0.wireOp",EDGE,"E209"),sQuery(id+"F0.wireOp",EDGE,"E210"),sQuery(id+"F0.wireOp",EDGE,"E211"),sQuery(id+"F0.wireOp",EDGE,"E212"),sQuery(id+"F0.wireOp",EDGE,"E213"),sQuery(id+"F0.wireOp",EDGE,"E214"),sQuery(id+"F0.wireOp",EDGE,"E215"),sQuery(id+"F0.wireOp",EDGE,"E216"),sQuery(id+"F0.wireOp",EDGE,"E217"),sQuery(id+"F0.wireOp",EDGE,"E218"),sQuery(id+"F0.wireOp",EDGE,"E219"),sQuery(id+"F0.wireOp",EDGE,"E220"),sQuery(id+"F0.wireOp",EDGE,"E221"),sQuery(id+"F0.wireOp",EDGE,"E222"),sQuery(id+"F0.wireOp",EDGE,"E223"),sQuery(id+"F0.wireOp",EDGE,"E224"),sQuery(id+"F0.wireOp",EDGE,"E225"),sQuery(id+"F0.wireOp",EDGE,"E226"),sQuery(id+"F0.wireOp",EDGE,"E227"),sQuery(id+"F0.wireOp",EDGE,"E228"),sQuery(id+"F0.wireOp",EDGE,"E229"),sQuery(id+"F0.wireOp",EDGE,"E230")])]});
            var Q14;
            Q14=makeQuery(id+"F1.opExtrude","SWEPT_BODY",BODY,{"disambiguationData":[OSD([sQuery(id+"F0.wireOp",EDGE,"E199"),sQuery(id+"F0.wireOp",EDGE,"E200"),sQuery(id+"F0.wireOp",EDGE,"E201"),sQuery(id+"F0.wireOp",EDGE,"E202"),sQuery(id+"F0.wireOp",EDGE,"E203"),sQuery(id+"F0.wireOp",EDGE,"E204"),sQuery(id+"F0.wireOp",EDGE,"E205"),sQuery(id+"F0.wireOp",EDGE,"E206")])]});
            var Q15;
            Q15=makeQuery(id+"F1.opExtrude","SWEPT_BODY",BODY,{"disambiguationData":[OSD([sQuery(id+"F0.wireOp",EDGE,"E179"),sQuery(id+"F0.wireOp",EDGE,"E180"),sQuery(id+"F0.wireOp",EDGE,"E181"),sQuery(id+"F0.wireOp",EDGE,"E182"),sQuery(id+"F0.wireOp",EDGE,"E183"),sQuery(id+"F0.wireOp",EDGE,"E184"),sQuery(id+"F0.wireOp",EDGE,"E185"),sQuery(id+"F0.wireOp",EDGE,"E186"),sQuery(id+"F0.wireOp",EDGE,"E187"),sQuery(id+"F0.wireOp",EDGE,"E188"),sQuery(id+"F0.wireOp",EDGE,"E189"),sQuery(id+"F0.wireOp",EDGE,"E190"),sQuery(id+"F0.wireOp",EDGE,"E191"),sQuery(id+"F0.wireOp",EDGE,"E192"),sQuery(id+"F0.wireOp",EDGE,"E193"),sQuery(id+"F0.wireOp",EDGE,"E194"),sQuery(id+"F0.wireOp",EDGE,"E195"),sQuery(id+"F0.wireOp",EDGE,"E196"),sQuery(id+"F0.wireOp",EDGE,"E197"),sQuery(id+"F0.wireOp",EDGE,"E198")])]});
            var Q16;
            Q16=makeQuery(id+"F1.opExtrude","SWEPT_BODY",BODY,{"disambiguationData":[OSD([sQuery(id+"F0.wireOp",EDGE,"E151"),sQuery(id+"F0.wireOp",EDGE,"E152"),sQuery(id+"F0.wireOp",EDGE,"E153"),sQuery(id+"F0.wireOp",EDGE,"E154"),sQuery(id+"F0.wireOp",EDGE,"E155"),sQuery(id+"F0.wireOp",EDGE,"E156"),sQuery(id+"F0.wireOp",EDGE,"E157"),sQuery(id+"F0.wireOp",EDGE,"E158"),sQuery(id+"F0.wireOp",EDGE,"E159"),sQuery(id+"F0.wireOp",EDGE,"E160"),sQuery(id+"F0.wireOp",EDGE,"E161"),sQuery(id+"F0.wireOp",EDGE,"E162")])]});
            var Q17;
            Q17=makeQuery(id+"F1.opExtrude","SWEPT_BODY",BODY,{"disambiguationData":[OSD([sQuery(id+"F0.wireOp",EDGE,"E163"),sQuery(id+"F0.wireOp",EDGE,"E164"),sQuery(id+"F0.wireOp",EDGE,"E165"),sQuery(id+"F0.wireOp",EDGE,"E166"),sQuery(id+"F0.wireOp",EDGE,"E167"),sQuery(id+"F0.wireOp",EDGE,"E168"),sQuery(id+"F0.wireOp",EDGE,"E169"),sQuery(id+"F0.wireOp",EDGE,"E170"),sQuery(id+"F0.wireOp",EDGE,"E171"),sQuery(id+"F0.wireOp",EDGE,"E172"),sQuery(id+"F0.wireOp",EDGE,"E173"),sQuery(id+"F0.wireOp",EDGE,"E174"),sQuery(id+"F0.wireOp",EDGE,"E175"),sQuery(id+"F0.wireOp",EDGE,"E176"),sQuery(id+"F0.wireOp",EDGE,"E177"),sQuery(id+"F0.wireOp",EDGE,"E178")])]});
            var Q18;
            Q18=makeQuery(id+"F1.opExtrude","SWEPT_BODY",BODY,{"disambiguationData":[OSD([sQuery(id+"F0.wireOp",EDGE,"E135"),sQuery(id+"F0.wireOp",EDGE,"E136"),sQuery(id+"F0.wireOp",EDGE,"E137"),sQuery(id+"F0.wireOp",EDGE,"E138"),sQuery(id+"F0.wireOp",EDGE,"E139"),sQuery(id+"F0.wireOp",EDGE,"E140"),sQuery(id+"F0.wireOp",EDGE,"E141"),sQuery(id+"F0.wireOp",EDGE,"E142"),sQuery(id+"F0.wireOp",EDGE,"E143"),sQuery(id+"F0.wireOp",EDGE,"E144"),sQuery(id+"F0.wireOp",EDGE,"E145"),sQuery(id+"F0.wireOp",EDGE,"E146"),sQuery(id+"F0.wireOp",EDGE,"E147"),sQuery(id+"F0.wireOp",EDGE,"E148"),sQuery(id+"F0.wireOp",EDGE,"E149"),sQuery(id+"F0.wireOp",EDGE,"E150")])]});
            var Q19;
            Q19=makeQuery(id+"F1.opExtrude","SWEPT_BODY",BODY,{"disambiguationData":[OSD([sQuery(id+"F0.wireOp",EDGE,"E119"),sQuery(id+"F0.wireOp",EDGE,"E120"),sQuery(id+"F0.wireOp",EDGE,"E121"),sQuery(id+"F0.wireOp",EDGE,"E122"),sQuery(id+"F0.wireOp",EDGE,"E123"),sQuery(id+"F0.wireOp",EDGE,"E124"),sQuery(id+"F0.wireOp",EDGE,"E125"),sQuery(id+"F0.wireOp",EDGE,"E126"),sQuery(id+"F0.wireOp",EDGE,"E127"),sQuery(id+"F0.wireOp",EDGE,"E128"),sQuery(id+"F0.wireOp",EDGE,"E129"),sQuery(id+"F0.wireOp",EDGE,"E130"),sQuery(id+"F0.wireOp",EDGE,"E131"),sQuery(id+"F0.wireOp",EDGE,"E132"),sQuery(id+"F0.wireOp",EDGE,"E133"),sQuery(id+"F0.wireOp",EDGE,"E134")])]});
            var Q20;
            Q20=makeQuery(id+"F1.opExtrude","SWEPT_BODY",BODY,{"disambiguationData":[OSD([sQuery(id+"F0.wireOp",EDGE,"E95"),sQuery(id+"F0.wireOp",EDGE,"E96"),sQuery(id+"F0.wireOp",EDGE,"E97"),sQuery(id+"F0.wireOp",EDGE,"E98"),sQuery(id+"F0.wireOp",EDGE,"E99"),sQuery(id+"F0.wireOp",EDGE,"E100"),sQuery(id+"F0.wireOp",EDGE,"E101"),sQuery(id+"F0.wireOp",EDGE,"E102"),sQuery(id+"F0.wireOp",EDGE,"E103"),sQuery(id+"F0.wireOp",EDGE,"E104"),sQuery(id+"F0.wireOp",EDGE,"E105"),sQuery(id+"F0.wireOp",EDGE,"E106"),sQuery(id+"F0.wireOp",EDGE,"E107"),sQuery(id+"F0.wireOp",EDGE,"E108"),sQuery(id+"F0.wireOp",EDGE,"E109"),sQuery(id+"F0.wireOp",EDGE,"E110"),sQuery(id+"F0.wireOp",EDGE,"E111"),sQuery(id+"F0.wireOp",EDGE,"E112"),sQuery(id+"F0.wireOp",EDGE,"E113"),sQuery(id+"F0.wireOp",EDGE,"E114"),sQuery(id+"F0.wireOp",EDGE,"E115"),sQuery(id+"F0.wireOp",EDGE,"E116"),sQuery(id+"F0.wireOp",EDGE,"E117"),sQuery(id+"F0.wireOp",EDGE,"E118")])]});
            var Q21;
            Q21=makeQuery(id+"F1.opExtrude","SWEPT_BODY",BODY,{"disambiguationData":[OSD([sQuery(id+"F0.wireOp",EDGE,"E79"),sQuery(id+"F0.wireOp",EDGE,"E80"),sQuery(id+"F0.wireOp",EDGE,"E81"),sQuery(id+"F0.wireOp",EDGE,"E82"),sQuery(id+"F0.wireOp",EDGE,"E83"),sQuery(id+"F0.wireOp",EDGE,"E84"),sQuery(id+"F0.wireOp",EDGE,"E85"),sQuery(id+"F0.wireOp",EDGE,"E86"),sQuery(id+"F0.wireOp",EDGE,"E87"),sQuery(id+"F0.wireOp",EDGE,"E88"),sQuery(id+"F0.wireOp",EDGE,"E89"),sQuery(id+"F0.wireOp",EDGE,"E90"),sQuery(id+"F0.wireOp",EDGE,"E91"),sQuery(id+"F0.wireOp",EDGE,"E92"),sQuery(id+"F0.wireOp",EDGE,"E93"),sQuery(id+"F0.wireOp",EDGE,"E94")])]});
            var Q22;
            Q22=makeQuery(id+"F1.opExtrude","SWEPT_BODY",BODY,{"disambiguationData":[OSD([sQuery(id+"F0.wireOp",EDGE,"E55"),sQuery(id+"F0.wireOp",EDGE,"E56"),sQuery(id+"F0.wireOp",EDGE,"E57"),sQuery(id+"F0.wireOp",EDGE,"E58"),sQuery(id+"F0.wireOp",EDGE,"E59"),sQuery(id+"F0.wireOp",EDGE,"E60"),sQuery(id+"F0.wireOp",EDGE,"E61"),sQuery(id+"F0.wireOp",EDGE,"E62"),sQuery(id+"F0.wireOp",EDGE,"E63"),sQuery(id+"F0.wireOp",EDGE,"E64"),sQuery(id+"F0.wireOp",EDGE,"E65"),sQuery(id+"F0.wireOp",EDGE,"E66"),sQuery(id+"F0.wireOp",EDGE,"E67"),sQuery(id+"F0.wireOp",EDGE,"E68"),sQuery(id+"F0.wireOp",EDGE,"E69"),sQuery(id+"F0.wireOp",EDGE,"E70"),sQuery(id+"F0.wireOp",EDGE,"E71"),sQuery(id+"F0.wireOp",EDGE,"E72"),sQuery(id+"F0.wireOp",EDGE,"E73"),sQuery(id+"F0.wireOp",EDGE,"E74"),sQuery(id+"F0.wireOp",EDGE,"E75"),sQuery(id+"F0.wireOp",EDGE,"E76"),sQuery(id+"F0.wireOp",EDGE,"E77"),sQuery(id+"F0.wireOp",EDGE,"E78")])]});
            var Q23;
            Q23=makeQuery(id+"F1.opExtrude","SWEPT_BODY",BODY,{"disambiguationData":[OSD([sQuery(id+"F0.wireOp",EDGE,"E39"),sQuery(id+"F0.wireOp",EDGE,"E40"),sQuery(id+"F0.wireOp",EDGE,"E41"),sQuery(id+"F0.wireOp",EDGE,"E42"),sQuery(id+"F0.wireOp",EDGE,"E43"),sQuery(id+"F0.wireOp",EDGE,"E44"),sQuery(id+"F0.wireOp",EDGE,"E45"),sQuery(id+"F0.wireOp",EDGE,"E46"),sQuery(id+"F0.wireOp",EDGE,"E47"),sQuery(id+"F0.wireOp",EDGE,"E48"),sQuery(id+"F0.wireOp",EDGE,"E49"),sQuery(id+"F0.wireOp",EDGE,"E50"),sQuery(id+"F0.wireOp",EDGE,"E51"),sQuery(id+"F0.wireOp",EDGE,"E52"),sQuery(id+"F0.wireOp",EDGE,"E53"),sQuery(id+"F0.wireOp",EDGE,"E54")])]});
            var Q24;
            Q24=makeQuery(id+"F1.opExtrude","SWEPT_BODY",BODY,{"disambiguationData":[OSD([sQuery(id+"F0.wireOp",EDGE,"E31"),sQuery(id+"F0.wireOp",EDGE,"E32"),sQuery(id+"F0.wireOp",EDGE,"E33"),sQuery(id+"F0.wireOp",EDGE,"E34"),sQuery(id+"F0.wireOp",EDGE,"E35"),sQuery(id+"F0.wireOp",EDGE,"E36"),sQuery(id+"F0.wireOp",EDGE,"E37"),sQuery(id+"F0.wireOp",EDGE,"E38")])]});
            var Q25;
            Q25=makeQuery(id+"F1.opExtrude","SWEPT_BODY",BODY,{"disambiguationData":[OSD([sQuery(id+"F0.wireOp",EDGE,"E343"),sQuery(id+"F0.wireOp",EDGE,"E344"),sQuery(id+"F0.wireOp",EDGE,"E345"),sQuery(id+"F0.wireOp",EDGE,"E346"),sQuery(id+"F0.wireOp",EDGE,"E347"),sQuery(id+"F0.wireOp",EDGE,"E348"),sQuery(id+"F0.wireOp",EDGE,"E349"),sQuery(id+"F0.wireOp",EDGE,"E350"),sQuery(id+"F0.wireOp",EDGE,"E351"),sQuery(id+"F0.wireOp",EDGE,"E352"),sQuery(id+"F0.wireOp",EDGE,"E353"),sQuery(id+"F0.wireOp",EDGE,"E354"),sQuery(id+"F0.wireOp",EDGE,"E355"),sQuery(id+"F0.wireOp",EDGE,"E356"),sQuery(id+"F0.wireOp",EDGE,"E357"),sQuery(id+"F0.wireOp",EDGE,"E358"),sQuery(id+"F0.wireOp",EDGE,"E359"),sQuery(id+"F0.wireOp",EDGE,"E360"),sQuery(id+"F0.wireOp",EDGE,"E361"),sQuery(id+"F0.wireOp",EDGE,"E362")])]});
            var Q26;
            Q26=makeQuery(id+"F1.opExtrude","SWEPT_BODY",BODY,{"disambiguationData":[OSD([sQuery(id+"F0.wireOp",EDGE,"E363"),sQuery(id+"F0.wireOp",EDGE,"E364"),sQuery(id+"F0.wireOp",EDGE,"E365"),sQuery(id+"F0.wireOp",EDGE,"E366"),sQuery(id+"F0.wireOp",EDGE,"E367"),sQuery(id+"F0.wireOp",EDGE,"E368"),sQuery(id+"F0.wireOp",EDGE,"E369"),sQuery(id+"F0.wireOp",EDGE,"E370"),sQuery(id+"F0.wireOp",EDGE,"E371"),sQuery(id+"F0.wireOp",EDGE,"E372"),sQuery(id+"F0.wireOp",EDGE,"E373"),sQuery(id+"F0.wireOp",EDGE,"E374"),sQuery(id+"F0.wireOp",EDGE,"E375"),sQuery(id+"F0.wireOp",EDGE,"E376"),sQuery(id+"F0.wireOp",EDGE,"E377"),sQuery(id+"F0.wireOp",EDGE,"E378"),sQuery(id+"F0.wireOp",EDGE,"E379"),sQuery(id+"F0.wireOp",EDGE,"E380"),sQuery(id+"F0.wireOp",EDGE,"E381"),sQuery(id+"F0.wireOp",EDGE,"E382"),sQuery(id+"F0.wireOp",EDGE,"E383"),sQuery(id+"F0.wireOp",EDGE,"E384"),sQuery(id+"F0.wireOp",EDGE,"E385"),sQuery(id+"F0.wireOp",EDGE,"E386")])]});
            var Q27;
            Q27=makeQuery(id+"F4.opExtrude","SWEPT_BODY",BODY,{"disambiguationData":[OSD([sQuery(id+"F0.wireOp",EDGE,"E0"),sQuery(id+"F0.wireOp",EDGE,"E1"),sQuery(id+"F0.wireOp",EDGE,"E2"),sQuery(id+"F0.wireOp",EDGE,"E3"),sQuery(id+"F0.wireOp",EDGE,"E4"),sQuery(id+"F0.wireOp",EDGE,"E5"),sQuery(id+"F0.wireOp",EDGE,"E6"),sQuery(id+"F0.wireOp",EDGE,"E7"),sQuery(id+"F0.wireOp",EDGE,"E8"),sQuery(id+"F0.wireOp",EDGE,"E9"),sQuery(id+"F0.wireOp",EDGE,"E10"),sQuery(id+"F0.wireOp",EDGE,"E11"),sQuery(id+"F0.wireOp",EDGE,"E12"),sQuery(id+"F0.wireOp",EDGE,"E13"),sQuery(id+"F0.wireOp",EDGE,"E14"),sQuery(id+"F0.wireOp",EDGE,"E15"),sQuery(id+"F0.wireOp",EDGE,"E16"),sQuery(id+"F0.wireOp",EDGE,"E17"),sQuery(id+"F0.wireOp",EDGE,"E18"),sQuery(id+"F0.wireOp",EDGE,"E19"),sQuery(id+"F0.wireOp",EDGE,"E20"),sQuery(id+"F0.wireOp",EDGE,"E21"),sQuery(id+"F0.wireOp",EDGE,"E22"),sQuery(id+"F0.wireOp",EDGE,"E23"),sQuery(id+"F0.wireOp",EDGE,"E24"),sQuery(id+"F0.wireOp",EDGE,"E25"),sQuery(id+"F0.wireOp",EDGE,"E26"),sQuery(id+"F0.wireOp",EDGE,"E27"),sQuery(id+"F0.wireOp",EDGE,"E28"),sQuery(id+"F0.wireOp",EDGE,"E29")])]});
            var Q28;
            Q28=makeQuery(id+"F4.opExtrude","SWEPT_BODY",BODY,{"disambiguationData":[OSD([sQuery(id+"F0.wireOp",EDGE,"E255"),sQuery(id+"F0.wireOp",EDGE,"E256"),sQuery(id+"F0.wireOp",EDGE,"E257"),sQuery(id+"F0.wireOp",EDGE,"E258"),sQuery(id+"F0.wireOp",EDGE,"E259"),sQuery(id+"F0.wireOp",EDGE,"E260")])]});
            var Q29;
            Q29=sQuery(id+"F0.wireOp",VERTEX,"E535.top.end");
            transform(context, id + "F5", {"entities" : qUnion([Q0, Q1, Q2, Q3, Q4, Q5, Q6, Q7, Q8, Q9, Q10, Q11, Q12, Q13, Q14, Q15, Q16, Q17, Q18, Q19, Q20, Q21, Q22, Q23, Q24, Q25, Q26, Q27, Q28]), "transformType" : TransformType.SCALE_UNIFORMLY, "scale" : 0.56, "scalePoint" : qUnion([Q29]), "makeCopy" : false});
        }
    });
